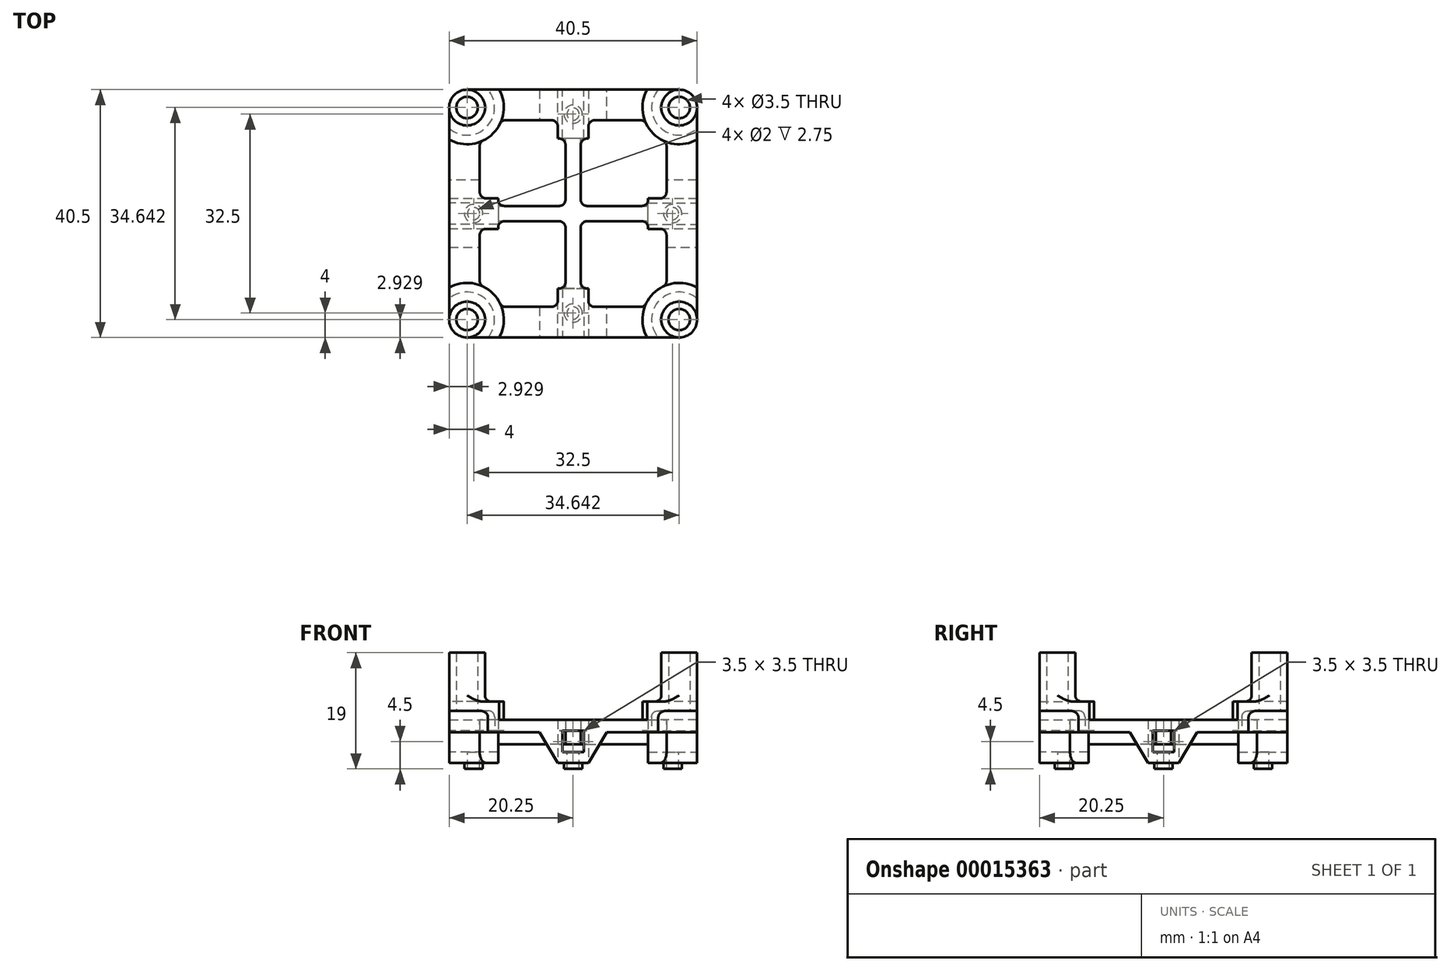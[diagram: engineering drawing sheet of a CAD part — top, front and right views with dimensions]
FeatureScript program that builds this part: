
annotation { "Feature Type Name" : "Feature", "Feature Type Description" : "" }
export const myFeature = defineFeature(function(context is Context, id is Id, definition is map)
    precondition{}
    {
        {
            var Q0;
            Q0=qCreatedBy(makeId("Top.planeOp"),FACE);
            var sketch = newSketch(context, id + "F0", { "sketchPlane" : qUnion([Q0])});
            skLineSegment(sketch, "E0.top", {"start": v(2.93, 40.5) * mm, "end": v(37.57, 40.5) * mm});
            skLineSegment(sketch, "E0.left", {"start": v(0, 2.93) * mm, "end": v(0, 37.57) * mm});
            skLineSegment(sketch, "E0.right", {"start": v(40.5, 2.93) * mm, "end": v(40.5, 37.57) * mm});
            skLineSegment(sketch, "E1", {"start": v(2.93, 0) * mm, "end": v(5, 0) * mm, "construction": true});
            skLineSegment(sketch, "E2", {"start": v(5, 0) * mm, "end": v(5, 5) * mm, "construction": true});
            skLineSegment(sketch, "E3.MirrorCS", {"start": v(40.5, 35.5) * mm, "end": v(35.5, 35.5) * mm, "construction": true});
            skLineSegment(sketch, "E4.MirrorCS", {"start": v(40.5, 37.57) * mm, "end": v(40.5, 35.5) * mm, "construction": true});
            skLineSegment(sketch, "E5", {"start": v(5, 35.5) * mm, "end": v(0, 40.5) * mm, "construction": true});
            skCircle(sketch, "E6", {"center": v(2.93, 37.57) * mm, "radius": 2.93 * mm});
            skLineSegment(sketch, "E7", {"start": v(35.5, 35.5) * mm, "end": v(40.5, 40.5) * mm, "construction": true});
            skLineSegment(sketch, "E8", {"start": v(35.5, 5) * mm, "end": v(40.5, 0) * mm, "construction": true});
            skLineSegment(sketch, "E9", {"start": v(5, 5) * mm, "end": v(0, 0) * mm, "construction": true});
            skCircle(sketch, "E10", {"center": v(37.57, 37.57) * mm, "radius": 2.93 * mm});
            skCircle(sketch, "E11", {"center": v(37.57, 2.93) * mm, "radius": 2.93 * mm});
            skCircle(sketch, "E12", {"center": v(2.93, 2.93) * mm, "radius": 2.93 * mm});
            skPoint(sketch, "E13.orphan", {"position": v(40.5, 40.5) * mm});
            skLineSegment(sketch, "E14", {"start": v(22.75, 35.5) * mm, "end": v(22.75, 35.5) * mm});
            skLineSegment(sketch, "E15", {"start": v(5, 35.5) * mm, "end": v(5, 22.75) * mm});
            skLineSegment(sketch, "E16", {"start": v(5, 5) * mm, "end": v(17.75, 5) * mm});
            skLineSegment(sketch, "E17", {"start": v(35.5, 35.5) * mm, "end": v(35.5, 22.75) * mm});
            skLineSegment(sketch, "E18", {"start": v(35.5, 35.5) * mm, "end": v(22.75, 35.5) * mm});
            skLineSegment(sketch, "E19.left", {"start": v(5, 5) * mm, "end": v(5, 17.75) * mm});
            skLineSegment(sketch, "E20.bottom", {"start": v(5, 35.5) * mm, "end": v(17.75, 35.5) * mm});
            skLineSegment(sketch, "E21.bottom", {"start": v(35.5, 5) * mm, "end": v(22.75, 5) * mm});
            skLineSegment(sketch, "E21.left", {"start": v(35.5, 5) * mm, "end": v(35.5, 17.75) * mm});
            skLineSegment(sketch, "E22.trimOffspring", {"start": v(35.5, 17.75) * mm, "end": v(35.5, 5) * mm});
            skLineSegment(sketch, "E23.trimOffspring", {"start": v(5, 17.75) * mm, "end": v(5, 5) * mm});
            skLineSegment(sketch, "E24.trimOffspring", {"start": v(17.75, 35.5) * mm, "end": v(5, 35.5) * mm});
            skLineSegment(sketch, "E25.trimOffspring", {"start": v(22.75, 5) * mm, "end": v(35.5, 5) * mm});
            skPoint(sketch, "E26.orphan", {"position": v(20.25, 0) * mm});
            skLineSegment(sketch, "E27", {"start": v(2.93, 0) * mm, "end": v(40.5, 0) * mm});
            skLineSegment(sketch, "E28", {"start": v(22.75, 5) * mm, "end": v(17.75, 5) * mm});
            skLineSegment(sketch, "E29", {"start": v(5, 22.75) * mm, "end": v(5, 17.75) * mm});
            skLineSegment(sketch, "E30", {"start": v(17.75, 35.5) * mm, "end": v(22.75, 35.5) * mm});
            skLineSegment(sketch, "E31", {"start": v(35.5, 22.75) * mm, "end": v(35.5, 17.75) * mm});
            skSolve(sketch);
        }
        {
            var Q0;
            Q0=qSketchRegion(id+"F0",true);
            extrude(context, id + "F1", {"entities" : qUnion([Q0]), "depth" : 2 * mm});
        }
        {
            var Q0;
            Q0=makeQuery(id+"F1.opExtrude","CAP_FACE",FACE,{"disambiguationData":[OSD([sQuery(id+"F0.wireOp",EDGE,"E0.top"),sQuery(id+"F0.wireOp",EDGE,"E0.left"),sQuery(id+"F0.wireOp",EDGE,"E0.right"),sQuery(id+"F0.wireOp",EDGE,"E6"),sQuery(id+"F0.wireOp",EDGE,"E10"),sQuery(id+"F0.wireOp",EDGE,"E11"),sQuery(id+"F0.wireOp",EDGE,"E12"),sQuery(id+"F0.wireOp",EDGE,"E16"),sQuery(id+"F0.wireOp",EDGE,"E15"),sQuery(id+"F0.wireOp",EDGE,"E18"),sQuery(id+"F0.wireOp",EDGE,"E17"),sQuery(id+"F0.wireOp",EDGE,"E22.trimOffspring"),sQuery(id+"F0.wireOp",EDGE,"E23.trimOffspring"),sQuery(id+"F0.wireOp",EDGE,"E24.trimOffspring"),sQuery(id+"F0.wireOp",EDGE,"E25.trimOffspring"),sQuery(id+"F0.wireOp",EDGE,"E27"),sQuery(id+"F0.wireOp",EDGE,"E28"),sQuery(id+"F0.wireOp",EDGE,"E29"),sQuery(id+"F0.wireOp",EDGE,"E30"),sQuery(id+"F0.wireOp",EDGE,"E31")])],"isStart":false});
            var sketch = newSketch(context, id + "F2", { "sketchPlane" : qUnion([Q0])});
            skLineSegment(sketch, "E32", {"start": v(20.25, 0) * mm, "end": v(20.25, 40.5) * mm, "construction": true});
            skLineSegment(sketch, "E33", {"start": v(0, 20.25) * mm, "end": v(40.5, 20.25) * mm, "construction": true});
            skLineSegment(sketch, "E34", {"start": v(17.75, 40.5) * mm, "end": v(22.75, 40.5) * mm});
            skLineSegment(sketch, "E35", {"start": v(0, 17.75) * mm, "end": v(0, 22.75) * mm});
            skLineSegment(sketch, "E36", {"start": v(17.75, 0) * mm, "end": v(22.75, 0) * mm});
            skLineSegment(sketch, "E37", {"start": v(40.5, 17.75) * mm, "end": v(40.5, 22.75) * mm});
            skLineSegment(sketch, "E38", {"start": v(40.5, 17.75) * mm, "end": v(22.75, 17.75) * mm});
            skLineSegment(sketch, "E39", {"start": v(22.75, 17.75) * mm, "end": v(22.75, 0) * mm});
            skLineSegment(sketch, "E40", {"start": v(17.75, 0) * mm, "end": v(17.75, 17.75) * mm});
            skLineSegment(sketch, "E41", {"start": v(17.75, 17.75) * mm, "end": v(0, 17.75) * mm});
            skLineSegment(sketch, "E42", {"start": v(0, 22.75) * mm, "end": v(17.75, 22.75) * mm});
            skLineSegment(sketch, "E43", {"start": v(17.75, 22.75) * mm, "end": v(17.75, 40.5) * mm});
            skLineSegment(sketch, "E44", {"start": v(22.75, 40.5) * mm, "end": v(22.75, 22.75) * mm});
            skLineSegment(sketch, "E45", {"start": v(22.75, 22.75) * mm, "end": v(40.5, 22.75) * mm});
            skSolve(sketch);
        }
        {
            var Q0;
            Q0=qSketchRegion(id+"F2",true);
            extrude(context, id + "F3", {"entities" : qUnion([Q0]), "operationType" : NewBodyOperationType.ADD, "oppositeDirection" : true, "depth" : 7 * mm});
        }
        {
            var Q0;
            Q0=makeQuery(id+"F3.boolean.opBoolean","MERGE",FACE,{"derivedFrom":[makeQuery(id+"F1.opExtrude","SWEPT_FACE",FACE,{"disambiguationData":[OSD([sQuery(id+"F0.wireOp",EDGE,"E27")])]}),makeQuery(id+"F3.opExtrude","SWEPT_FACE",FACE,{"disambiguationData":[OSD([sQuery(id+"F2.wireOp",EDGE,"E36")])]})]});
            var sketch = newSketch(context, id + "F4", { "sketchPlane" : qUnion([Q0])});
            skLineSegment(sketch, "E46", {"start": v(22.75, -5) * mm, "end": v(17.75, 2) * mm, "construction": true});
            skLineSegment(sketch, "E47", {"start": v(17.75, -5) * mm, "end": v(22.75, 2) * mm, "construction": true});
            skLineSegment(sketch, "E48.rect.bottom", {"start": v(18.5, -3.25) * mm, "end": v(22, -3.25) * mm});
            skLineSegment(sketch, "E48.rect.top", {"start": v(18.5, 0.25) * mm, "end": v(22, 0.25) * mm});
            skLineSegment(sketch, "E48.rect.left", {"start": v(18.5, -3.25) * mm, "end": v(18.5, 0.25) * mm});
            skLineSegment(sketch, "E48.rect.right", {"start": v(22, -3.25) * mm, "end": v(22, 0.25) * mm});
            skPoint(sketch, "E48.rect.middle", {"position": v(20.25, -1.5) * mm});
            skSolve(sketch);
        }
        {
            var Q0;
            Q0=qSketchRegion(id+"F4",true);
            extrude(context, id + "F5", {"entities" : qUnion([Q0]), "operationType" : NewBodyOperationType.REMOVE, "oppositeDirection" : true, "depth" : 8 * mm});
        }
        {
            var Q0;
            Q0=makeQuery(id+"F3.boolean.opBoolean","MERGE",FACE,{"derivedFrom":[makeQuery(id+"F1.opExtrude","SWEPT_FACE",FACE,{"disambiguationData":[OSD([sQuery(id+"F0.wireOp",EDGE,"E0.right")])]}),makeQuery(id+"F3.opExtrude","SWEPT_FACE",FACE,{"disambiguationData":[OSD([sQuery(id+"F2.wireOp",EDGE,"E37")])]})]});
            var sketch = newSketch(context, id + "F6", { "sketchPlane" : qUnion([Q0])});
            skLineSegment(sketch, "E49", {"start": v(17.75, -5) * mm, "end": v(22.75, 2) * mm, "construction": true});
            skLineSegment(sketch, "E50", {"start": v(22.75, -5) * mm, "end": v(17.75, 2) * mm, "construction": true});
            skLineSegment(sketch, "E51.rect.bottom", {"start": v(18.5, -3.25) * mm, "end": v(22, -3.25) * mm});
            skLineSegment(sketch, "E51.rect.top", {"start": v(18.5, 0.25) * mm, "end": v(22, 0.25) * mm});
            skLineSegment(sketch, "E51.rect.left", {"start": v(18.5, -3.25) * mm, "end": v(18.5, 0.25) * mm});
            skLineSegment(sketch, "E51.rect.right", {"start": v(22, -3.25) * mm, "end": v(22, 0.25) * mm});
            skPoint(sketch, "E51.rect.middle", {"position": v(20.25, -1.5) * mm});
            skSolve(sketch);
        }
        {
            var Q0;
            Q0=qSketchRegion(id+"F6",true);
            extrude(context, id + "F7", {"entities" : qUnion([Q0]), "operationType" : NewBodyOperationType.REMOVE, "oppositeDirection" : true, "depth" : 8 * mm});
        }
        {
            var Q0;
            Q0=makeQuery(id+"F3.boolean.opBoolean","MERGE",FACE,{"derivedFrom":[makeQuery(id+"F1.opExtrude","SWEPT_FACE",FACE,{"disambiguationData":[OSD([sQuery(id+"F0.wireOp",EDGE,"E0.top")])]}),makeQuery(id+"F3.opExtrude","SWEPT_FACE",FACE,{"disambiguationData":[OSD([sQuery(id+"F2.wireOp",EDGE,"E34")])]})]});
            var sketch = newSketch(context, id + "F8", { "sketchPlane" : qUnion([Q0])});
            skLineSegment(sketch, "E52", {"start": v(-17.75, -5) * mm, "end": v(-22.75, 2) * mm, "construction": true});
            skLineSegment(sketch, "E53", {"start": v(-22.75, -5) * mm, "end": v(-17.75, 2) * mm, "construction": true});
            skLineSegment(sketch, "E54.rect.bottom", {"start": v(-22, -3.25) * mm, "end": v(-18.5, -3.25) * mm});
            skLineSegment(sketch, "E54.rect.top", {"start": v(-22, 0.25) * mm, "end": v(-18.5, 0.25) * mm});
            skLineSegment(sketch, "E54.rect.left", {"start": v(-22, -3.25) * mm, "end": v(-22, 0.25) * mm});
            skLineSegment(sketch, "E54.rect.right", {"start": v(-18.5, -3.25) * mm, "end": v(-18.5, 0.25) * mm});
            skPoint(sketch, "E54.rect.middle", {"position": v(-20.25, -1.5) * mm});
            skSolve(sketch);
        }
        {
            var Q0;
            Q0=qSketchRegion(id+"F8",true);
            extrude(context, id + "F9", {"entities" : qUnion([Q0]), "operationType" : NewBodyOperationType.REMOVE, "oppositeDirection" : true, "depth" : 8 * mm});
        }
        {
            var Q0;
            Q0=makeQuery(id+"F3.boolean.opBoolean","MERGE",FACE,{"derivedFrom":[makeQuery(id+"F1.opExtrude","SWEPT_FACE",FACE,{"disambiguationData":[OSD([sQuery(id+"F0.wireOp",EDGE,"E0.left")])]}),makeQuery(id+"F3.opExtrude","SWEPT_FACE",FACE,{"disambiguationData":[OSD([sQuery(id+"F2.wireOp",EDGE,"E35")])]})]});
            var sketch = newSketch(context, id + "F10", { "sketchPlane" : qUnion([Q0])});
            skLineSegment(sketch, "E55", {"start": v(-22.75, -5) * mm, "end": v(-17.75, 2) * mm, "construction": true});
            skLineSegment(sketch, "E56", {"start": v(-17.75, -5) * mm, "end": v(-22.75, -1.43) * mm, "construction": true});
            skLineSegment(sketch, "E57.rect.bottom", {"start": v(-22, -3.25) * mm, "end": v(-18.5, -3.25) * mm});
            skLineSegment(sketch, "E57.rect.top", {"start": v(-22, 0.25) * mm, "end": v(-18.5, 0.25) * mm});
            skLineSegment(sketch, "E57.rect.left", {"start": v(-22, -3.25) * mm, "end": v(-22, 0.25) * mm});
            skLineSegment(sketch, "E57.rect.right", {"start": v(-18.5, -3.25) * mm, "end": v(-18.5, 0.25) * mm});
            skPoint(sketch, "E57.rect.middle", {"position": v(-20.25, -1.5) * mm});
            skSolve(sketch);
        }
        {
            var Q0;
            Q0=qSketchRegion(id+"F10",true);
            extrude(context, id + "F11", {"entities" : qUnion([Q0]), "operationType" : NewBodyOperationType.REMOVE, "oppositeDirection" : true, "depth" : 8 * mm});
        }
        {
            var Q0;
            Q0=makeQuery(id+"F3.opExtrude","CAP_FACE",FACE,{"disambiguationData":[OSD([sQuery(id+"F2.wireOp",EDGE,"E34"),sQuery(id+"F2.wireOp",EDGE,"E35"),sQuery(id+"F2.wireOp",EDGE,"E36"),sQuery(id+"F2.wireOp",EDGE,"E37"),sQuery(id+"F2.wireOp",EDGE,"E38"),sQuery(id+"F2.wireOp",EDGE,"E39"),sQuery(id+"F2.wireOp",EDGE,"E40"),sQuery(id+"F2.wireOp",EDGE,"E41"),sQuery(id+"F2.wireOp",EDGE,"E42"),sQuery(id+"F2.wireOp",EDGE,"E43"),sQuery(id+"F2.wireOp",EDGE,"E44"),sQuery(id+"F2.wireOp",EDGE,"E45")])],"isStart":false});
            var sketch = newSketch(context, id + "F12", { "sketchPlane" : qUnion([Q0])});
            skLineSegment(sketch, "E58", {"start": v(0, -22.75) * mm, "end": v(8, -22.75) * mm, "construction": true});
            skLineSegment(sketch, "E59", {"start": v(8, -22.75) * mm, "end": v(8, -17.75) * mm});
            skLineSegment(sketch, "E60", {"start": v(22.75, -40.5) * mm, "end": v(22.75, -32.5) * mm, "construction": true});
            skLineSegment(sketch, "E61", {"start": v(22.75, -32.5) * mm, "end": v(17.75, -32.5) * mm});
            skLineSegment(sketch, "E62", {"start": v(40.5, -17.75) * mm, "end": v(32.5, -17.75) * mm, "construction": true});
            skLineSegment(sketch, "E63", {"start": v(32.5, -17.75) * mm, "end": v(32.5, -22.75) * mm});
            skLineSegment(sketch, "E64", {"start": v(22.75, 0) * mm, "end": v(22.75, -8) * mm, "construction": true});
            skLineSegment(sketch, "E65", {"start": v(22.75, -8) * mm, "end": v(17.75, -8) * mm});
            skLineSegment(sketch, "E66", {"start": v(32.5, -22.75) * mm, "end": v(22.75, -22.75) * mm});
            skLineSegment(sketch, "E67", {"start": v(22.75, -22.75) * mm, "end": v(22.75, -32.5) * mm});
            skLineSegment(sketch, "E68", {"start": v(17.75, -32.5) * mm, "end": v(17.75, -22.75) * mm});
            skLineSegment(sketch, "E69", {"start": v(17.75, -22.75) * mm, "end": v(8, -22.75) * mm});
            skLineSegment(sketch, "E70", {"start": v(8, -17.75) * mm, "end": v(17.75, -17.75) * mm});
            skLineSegment(sketch, "E71", {"start": v(17.75, -17.75) * mm, "end": v(17.75, -8) * mm});
            skLineSegment(sketch, "E72", {"start": v(22.75, -8) * mm, "end": v(22.75, -17.75) * mm});
            skLineSegment(sketch, "E73", {"start": v(22.75, -17.75) * mm, "end": v(32.5, -17.75) * mm});
            skSolve(sketch);
        }
        {
            var Q0;
            Q0=qSketchRegion(id+"F12",true);
            extrude(context, id + "F13", {"entities" : qUnion([Q0]), "operationType" : NewBodyOperationType.REMOVE, "oppositeDirection" : true, "depth" : 3 * mm});
        }
        {
            var Q0;
            {var subQ0=sQuery(id+"F0.wireOp",EDGE,"E0.top");var subQ1=sQuery(id+"F0.wireOp",EDGE,"E0.left");var subQ2=sQuery(id+"F0.wireOp",EDGE,"E0.right");var subQ3=sQuery(id+"F0.wireOp",EDGE,"E6");var subQ4=sQuery(id+"F0.wireOp",EDGE,"E10");var subQ5=sQuery(id+"F0.wireOp",EDGE,"E11");var subQ6=sQuery(id+"F0.wireOp",EDGE,"E12");var subQ7=sQuery(id+"F0.wireOp",EDGE,"E16");var subQ8=sQuery(id+"F0.wireOp",EDGE,"E15");var subQ9=sQuery(id+"F0.wireOp",EDGE,"E18");var subQ10=sQuery(id+"F0.wireOp",EDGE,"E17");var subQ11=sQuery(id+"F0.wireOp",EDGE,"E22.trimOffspring");var subQ12=sQuery(id+"F0.wireOp",EDGE,"E23.trimOffspring");var subQ13=sQuery(id+"F0.wireOp",EDGE,"E24.trimOffspring");var subQ14=sQuery(id+"F0.wireOp",EDGE,"E25.trimOffspring");var subQ15=sQuery(id+"F0.wireOp",EDGE,"E27");var subQ16=sQuery(id+"F0.wireOp",EDGE,"E28");var subQ17=sQuery(id+"F0.wireOp",EDGE,"E29");var subQ18=sQuery(id+"F0.wireOp",EDGE,"E30");var subQ19=sQuery(id+"F0.wireOp",EDGE,"E31");var subQ20=sQuery(id+"F2.wireOp",EDGE,"E34");var subQ21=sQuery(id+"F2.wireOp",EDGE,"E35");var subQ22=sQuery(id+"F2.wireOp",EDGE,"E36");var subQ23=sQuery(id+"F2.wireOp",EDGE,"E37");var subQ24=sQuery(id+"F2.wireOp",EDGE,"E38");var subQ25=sQuery(id+"F2.wireOp",EDGE,"E39");var subQ26=sQuery(id+"F2.wireOp",EDGE,"E40");var subQ27=sQuery(id+"F2.wireOp",EDGE,"E41");var subQ28=sQuery(id+"F2.wireOp",EDGE,"E42");var subQ29=sQuery(id+"F2.wireOp",EDGE,"E43");var subQ30=sQuery(id+"F2.wireOp",EDGE,"E44");var subQ31=sQuery(id+"F2.wireOp",EDGE,"E45");Q0=makeQuery(id+"F5kflJwKjGJNZqC_1.boolean.opBoolean","SPLIT",FACE,{"disambiguationData":[TD([makeQuery(id+"F1.opExtrude","SWEPT_FACE",FACE,{"disambiguationData":[OSD([subQ0])]})])],"derivedFrom":makeQuery(id+"F3.boolean.opBoolean","MERGE",FACE,{"derivedFrom":[makeQuery(id+"F1.opExtrude","CAP_FACE",FACE,{"disambiguationData":[OSD([subQ0,subQ1,subQ2,subQ3,subQ4,subQ5,subQ6,subQ7,subQ8,subQ9,subQ10,subQ11,subQ12,subQ13,subQ14,subQ15,subQ16,subQ17,subQ18,subQ19])],"isStart":false}),makeQuery(id+"F3.opExtrude","CAP_FACE",FACE,{"disambiguationData":[OSD([subQ20,subQ21,subQ22,subQ23,subQ24,subQ25,subQ26,subQ27,subQ28,subQ29,subQ30,subQ31])],"isStart":true})]})});}
            var sketch = newSketch(context, id + "F14", { "sketchPlane" : qUnion([Q0])});
            skCircle(sketch, "E74", {"center": v(37.57, 37.57) * mm, "radius": 2.93 * mm});
            skCircle(sketch, "E75", {"center": v(37.57, 2.93) * mm, "radius": 2.93 * mm});
            skCircle(sketch, "E76", {"center": v(2.93, 2.93) * mm, "radius": 2.93 * mm});
            skCircle(sketch, "E77", {"center": v(2.93, 37.57) * mm, "radius": 2.93 * mm});
            skSolve(sketch);
        }
        {
            var Q0;
            Q0=qSketchRegion(id+"F14",true);
            extrude(context, id + "F15", {"entities" : qUnion([Q0]), "operationType" : NewBodyOperationType.ADD, "depth" : 11 * mm});
        }
        {
            var Q0;
            {var subQ0=sQuery(id+"F2.wireOp",EDGE,"E41");var subQ1=sQuery(id+"F2.wireOp",EDGE,"E35");var subQ2=sQuery(id+"F2.wireOp",EDGE,"E42");Q0=makeQuery(id+"F13.boolean.opBoolean","SPLIT",FACE,{"disambiguationData":[TD([makeQuery(id+"F1.opExtrude","SWEPT_FACE",FACE,{"disambiguationData":[OSD([sQuery(id+"F0.wireOp",EDGE,"E0.left")])]})])],"derivedFrom":makeQuery(id+"F3.opExtrude","CAP_FACE",FACE,{"disambiguationData":[OSD([sQuery(id+"F2.wireOp",EDGE,"E34"),subQ1,sQuery(id+"F2.wireOp",EDGE,"E36"),sQuery(id+"F2.wireOp",EDGE,"E37"),sQuery(id+"F2.wireOp",EDGE,"E38"),sQuery(id+"F2.wireOp",EDGE,"E39"),sQuery(id+"F2.wireOp",EDGE,"E40"),subQ0,subQ2,sQuery(id+"F2.wireOp",EDGE,"E43"),sQuery(id+"F2.wireOp",EDGE,"E44"),sQuery(id+"F2.wireOp",EDGE,"E45")])],"isStart":false})});}
            var sketch = newSketch(context, id + "F16", { "sketchPlane" : qUnion([Q0])});
            skLineSegment(sketch, "E78", {"start": v(8, -22.75) * mm, "end": v(0, -17.75) * mm, "construction": true});
            skCircle(sketch, "E79", {"center": v(4, -20.25) * mm, "radius": 1 * mm});
            skCircle(sketch, "E80", {"center": v(4, -20.25) * mm, "radius": 1.5 * mm});
            skSolve(sketch);
        }
        {
            var Q0;
            Q0=qSketchRegion(id+"F16",true);
            extrude(context, id + "F17", {"entities" : qUnion([Q0]), "operationType" : NewBodyOperationType.ADD, "depth" : 1 * mm});
        }
        {
            var Q0;
            {var subQ0=sQuery(id+"F2.wireOp",EDGE,"E43");var subQ1=sQuery(id+"F2.wireOp",EDGE,"E34");var subQ2=sQuery(id+"F2.wireOp",EDGE,"E44");Q0=makeQuery(id+"F13.boolean.opBoolean","SPLIT",FACE,{"disambiguationData":[TD([makeQuery(id+"F1.opExtrude","SWEPT_FACE",FACE,{"disambiguationData":[OSD([sQuery(id+"F0.wireOp",EDGE,"E0.top")])]})])],"derivedFrom":makeQuery(id+"F3.opExtrude","CAP_FACE",FACE,{"disambiguationData":[OSD([subQ1,sQuery(id+"F2.wireOp",EDGE,"E35"),sQuery(id+"F2.wireOp",EDGE,"E36"),sQuery(id+"F2.wireOp",EDGE,"E37"),sQuery(id+"F2.wireOp",EDGE,"E38"),sQuery(id+"F2.wireOp",EDGE,"E39"),sQuery(id+"F2.wireOp",EDGE,"E40"),sQuery(id+"F2.wireOp",EDGE,"E41"),sQuery(id+"F2.wireOp",EDGE,"E42"),subQ0,subQ2,sQuery(id+"F2.wireOp",EDGE,"E45")])],"isStart":false})});}
            var sketch = newSketch(context, id + "F18", { "sketchPlane" : qUnion([Q0])});
            skLineSegment(sketch, "E81", {"start": v(22.75, -32.5) * mm, "end": v(17.75, -40.5) * mm});
            skCircle(sketch, "E82", {"center": v(20.25, -36.5) * mm, "radius": 1 * mm});
            skCircle(sketch, "E83", {"center": v(20.25, -36.5) * mm, "radius": 1.5 * mm});
            skSolve(sketch);
        }
        {
            var Q0;
            Q0=qSketchRegion(id+"F18",true);
            extrude(context, id + "F19", {"entities" : qUnion([Q0]), "operationType" : NewBodyOperationType.ADD, "depth" : 1 * mm});
        }
        {
            var Q0;
            {var subQ0=sQuery(id+"F2.wireOp",EDGE,"E45");var subQ1=sQuery(id+"F2.wireOp",EDGE,"E37");var subQ2=sQuery(id+"F2.wireOp",EDGE,"E38");Q0=makeQuery(id+"F13.boolean.opBoolean","SPLIT",FACE,{"disambiguationData":[TD([makeQuery(id+"F1.opExtrude","SWEPT_FACE",FACE,{"disambiguationData":[OSD([sQuery(id+"F0.wireOp",EDGE,"E0.right")])]})])],"derivedFrom":makeQuery(id+"F3.opExtrude","CAP_FACE",FACE,{"disambiguationData":[OSD([sQuery(id+"F2.wireOp",EDGE,"E34"),sQuery(id+"F2.wireOp",EDGE,"E35"),sQuery(id+"F2.wireOp",EDGE,"E36"),subQ1,subQ2,sQuery(id+"F2.wireOp",EDGE,"E39"),sQuery(id+"F2.wireOp",EDGE,"E40"),sQuery(id+"F2.wireOp",EDGE,"E41"),sQuery(id+"F2.wireOp",EDGE,"E42"),sQuery(id+"F2.wireOp",EDGE,"E43"),sQuery(id+"F2.wireOp",EDGE,"E44"),subQ0])],"isStart":false})});}
            var sketch = newSketch(context, id + "F20", { "sketchPlane" : qUnion([Q0])});
            skLineSegment(sketch, "E84", {"start": v(32.5, -17.75) * mm, "end": v(40.5, -22.75) * mm});
            skCircle(sketch, "E85", {"center": v(36.5, -20.25) * mm, "radius": 1 * mm});
            skCircle(sketch, "E86", {"center": v(36.5, -20.25) * mm, "radius": 1.5 * mm});
            skSolve(sketch);
        }
        {
            var Q0;
            Q0=qSketchRegion(id+"F20",true);
            extrude(context, id + "F21", {"entities" : qUnion([Q0]), "operationType" : NewBodyOperationType.ADD, "depth" : 1 * mm});
        }
        {
            var Q0;
            {var subQ0=sQuery(id+"F2.wireOp",EDGE,"E40");var subQ1=sQuery(id+"F2.wireOp",EDGE,"E39");var subQ2=sQuery(id+"F2.wireOp",EDGE,"E36");Q0=makeQuery(id+"F13.boolean.opBoolean","SPLIT",FACE,{"disambiguationData":[TD([makeQuery(id+"F1.opExtrude","SWEPT_FACE",FACE,{"disambiguationData":[OSD([sQuery(id+"F0.wireOp",EDGE,"E27")])]})])],"derivedFrom":makeQuery(id+"F3.opExtrude","CAP_FACE",FACE,{"disambiguationData":[OSD([sQuery(id+"F2.wireOp",EDGE,"E34"),sQuery(id+"F2.wireOp",EDGE,"E35"),subQ2,sQuery(id+"F2.wireOp",EDGE,"E37"),sQuery(id+"F2.wireOp",EDGE,"E38"),subQ1,subQ0,sQuery(id+"F2.wireOp",EDGE,"E41"),sQuery(id+"F2.wireOp",EDGE,"E42"),sQuery(id+"F2.wireOp",EDGE,"E43"),sQuery(id+"F2.wireOp",EDGE,"E44"),sQuery(id+"F2.wireOp",EDGE,"E45")])],"isStart":false})});}
            var sketch = newSketch(context, id + "F22", { "sketchPlane" : qUnion([Q0])});
            skLineSegment(sketch, "E87", {"start": v(17.75, -8) * mm, "end": v(22.75, 0) * mm});
            skCircle(sketch, "E88", {"center": v(20.25, -4) * mm, "radius": 1 * mm});
            skCircle(sketch, "E89", {"center": v(20.25, -4) * mm, "radius": 1.5 * mm});
            skSolve(sketch);
        }
        {
            var Q0;
            Q0=qSketchRegion(id+"F22",true);
            extrude(context, id + "F23", {"entities" : qUnion([Q0]), "operationType" : NewBodyOperationType.ADD, "depth" : 1 * mm});
        }
        {
            var Q0;
            {var subQ0=sQuery(id+"F0.wireOp",EDGE,"E0.left");var subQ1=sQuery(id+"F0.wireOp",EDGE,"E12");var subQ2=sQuery(id+"F0.wireOp",EDGE,"E16");var subQ3=sQuery(id+"F0.wireOp",EDGE,"E15");var subQ4=sQuery(id+"F0.wireOp",EDGE,"E23.trimOffspring");var subQ5=sQuery(id+"F0.wireOp",EDGE,"E25.trimOffspring");var subQ6=sQuery(id+"F0.wireOp",EDGE,"E27");var subQ7=sQuery(id+"F0.wireOp",EDGE,"E28");var subQ8=sQuery(id+"F0.wireOp",EDGE,"E29");Q0=makeQuery(id+"F3.boolean.opBoolean","SPLIT",FACE,{"disambiguationData":[TD([makeQuery(id+"F1.opExtrude","SWEPT_FACE",FACE,{"disambiguationData":[OSD([subQ1])]})])],"derivedFrom":makeQuery(id+"F1.opExtrude","CAP_FACE",FACE,{"disambiguationData":[OSD([sQuery(id+"F0.wireOp",EDGE,"E0.top"),subQ0,sQuery(id+"F0.wireOp",EDGE,"E0.right"),sQuery(id+"F0.wireOp",EDGE,"E6"),sQuery(id+"F0.wireOp",EDGE,"E10"),sQuery(id+"F0.wireOp",EDGE,"E11"),subQ1,subQ2,subQ3,sQuery(id+"F0.wireOp",EDGE,"E18"),sQuery(id+"F0.wireOp",EDGE,"E17"),sQuery(id+"F0.wireOp",EDGE,"E22.trimOffspring"),subQ4,sQuery(id+"F0.wireOp",EDGE,"E24.trimOffspring"),subQ5,subQ6,subQ7,subQ8,sQuery(id+"F0.wireOp",EDGE,"E30"),sQuery(id+"F0.wireOp",EDGE,"E31")])],"isStart":true})});}
            var sketch = newSketch(context, id + "F24", { "sketchPlane" : qUnion([Q0])});
            skCircle(sketch, "E90", {"center": v(2.93, -2.93) * mm, "radius": 1.75 * mm});
            skSolve(sketch);
        }
        {
            var Q0;
            Q0=qSketchRegion(id+"F24",true);
            extrude(context, id + "F25", {"entities" : qUnion([Q0]), "operationType" : NewBodyOperationType.REMOVE, "oppositeDirection" : true, "depth" : 25 * mm});
        }
        {
            var Q0;
            {var subQ0=sQuery(id+"F0.wireOp",EDGE,"E0.right");var subQ1=sQuery(id+"F0.wireOp",EDGE,"E11");var subQ2=sQuery(id+"F0.wireOp",EDGE,"E16");var subQ3=sQuery(id+"F0.wireOp",EDGE,"E17");var subQ4=sQuery(id+"F0.wireOp",EDGE,"E22.trimOffspring");var subQ5=sQuery(id+"F0.wireOp",EDGE,"E25.trimOffspring");var subQ6=sQuery(id+"F0.wireOp",EDGE,"E27");var subQ7=sQuery(id+"F0.wireOp",EDGE,"E28");var subQ8=sQuery(id+"F0.wireOp",EDGE,"E31");Q0=makeQuery(id+"F3.boolean.opBoolean","SPLIT",FACE,{"disambiguationData":[TD([makeQuery(id+"F1.opExtrude","SWEPT_FACE",FACE,{"disambiguationData":[OSD([subQ1])]})])],"derivedFrom":makeQuery(id+"F1.opExtrude","CAP_FACE",FACE,{"disambiguationData":[OSD([sQuery(id+"F0.wireOp",EDGE,"E0.top"),sQuery(id+"F0.wireOp",EDGE,"E0.left"),subQ0,sQuery(id+"F0.wireOp",EDGE,"E6"),sQuery(id+"F0.wireOp",EDGE,"E10"),subQ1,sQuery(id+"F0.wireOp",EDGE,"E12"),subQ2,sQuery(id+"F0.wireOp",EDGE,"E15"),sQuery(id+"F0.wireOp",EDGE,"E18"),subQ3,subQ4,sQuery(id+"F0.wireOp",EDGE,"E23.trimOffspring"),sQuery(id+"F0.wireOp",EDGE,"E24.trimOffspring"),subQ5,subQ6,subQ7,sQuery(id+"F0.wireOp",EDGE,"E29"),sQuery(id+"F0.wireOp",EDGE,"E30"),subQ8])],"isStart":true})});}
            var sketch = newSketch(context, id + "F26", { "sketchPlane" : qUnion([Q0])});
            skCircle(sketch, "E91", {"center": v(37.57, -2.93) * mm, "radius": 1.75 * mm});
            skSolve(sketch);
        }
        {
            var Q0;
            Q0=qSketchRegion(id+"F26",true);
            extrude(context, id + "F27", {"entities" : qUnion([Q0]), "operationType" : NewBodyOperationType.REMOVE, "oppositeDirection" : true, "depth" : 25 * mm});
        }
        {
            var Q0;
            {var subQ0=sQuery(id+"F0.wireOp",EDGE,"E0.top");var subQ1=sQuery(id+"F0.wireOp",EDGE,"E0.left");var subQ2=sQuery(id+"F0.wireOp",EDGE,"E6");var subQ3=sQuery(id+"F0.wireOp",EDGE,"E15");var subQ4=sQuery(id+"F0.wireOp",EDGE,"E18");var subQ5=sQuery(id+"F0.wireOp",EDGE,"E23.trimOffspring");var subQ6=sQuery(id+"F0.wireOp",EDGE,"E24.trimOffspring");var subQ7=sQuery(id+"F0.wireOp",EDGE,"E29");var subQ8=sQuery(id+"F0.wireOp",EDGE,"E30");Q0=makeQuery(id+"F3.boolean.opBoolean","SPLIT",FACE,{"disambiguationData":[TD([makeQuery(id+"F1.opExtrude","SWEPT_FACE",FACE,{"disambiguationData":[OSD([subQ2])]})])],"derivedFrom":makeQuery(id+"F1.opExtrude","CAP_FACE",FACE,{"disambiguationData":[OSD([subQ0,subQ1,sQuery(id+"F0.wireOp",EDGE,"E0.right"),subQ2,sQuery(id+"F0.wireOp",EDGE,"E10"),sQuery(id+"F0.wireOp",EDGE,"E11"),sQuery(id+"F0.wireOp",EDGE,"E12"),sQuery(id+"F0.wireOp",EDGE,"E16"),subQ3,subQ4,sQuery(id+"F0.wireOp",EDGE,"E17"),sQuery(id+"F0.wireOp",EDGE,"E22.trimOffspring"),subQ5,subQ6,sQuery(id+"F0.wireOp",EDGE,"E25.trimOffspring"),sQuery(id+"F0.wireOp",EDGE,"E27"),sQuery(id+"F0.wireOp",EDGE,"E28"),subQ7,subQ8,sQuery(id+"F0.wireOp",EDGE,"E31")])],"isStart":true})});}
            var sketch = newSketch(context, id + "F28", { "sketchPlane" : qUnion([Q0])});
            skCircle(sketch, "E92", {"center": v(2.93, -37.57) * mm, "radius": 1.75 * mm});
            skSolve(sketch);
        }
        {
            var Q0;
            Q0=qSketchRegion(id+"F28",true);
            extrude(context, id + "F29", {"entities" : qUnion([Q0]), "operationType" : NewBodyOperationType.REMOVE, "oppositeDirection" : true, "depth" : 25 * mm});
        }
        {
            var Q0;
            {var subQ0=sQuery(id+"F0.wireOp",EDGE,"E0.top");var subQ1=sQuery(id+"F0.wireOp",EDGE,"E0.right");var subQ2=sQuery(id+"F0.wireOp",EDGE,"E10");var subQ3=sQuery(id+"F0.wireOp",EDGE,"E18");var subQ4=sQuery(id+"F0.wireOp",EDGE,"E17");var subQ5=sQuery(id+"F0.wireOp",EDGE,"E22.trimOffspring");var subQ6=sQuery(id+"F0.wireOp",EDGE,"E24.trimOffspring");var subQ7=sQuery(id+"F0.wireOp",EDGE,"E30");var subQ8=sQuery(id+"F0.wireOp",EDGE,"E31");Q0=makeQuery(id+"F3.boolean.opBoolean","SPLIT",FACE,{"disambiguationData":[TD([makeQuery(id+"F1.opExtrude","SWEPT_FACE",FACE,{"disambiguationData":[OSD([subQ2])]})])],"derivedFrom":makeQuery(id+"F1.opExtrude","CAP_FACE",FACE,{"disambiguationData":[OSD([subQ0,sQuery(id+"F0.wireOp",EDGE,"E0.left"),subQ1,sQuery(id+"F0.wireOp",EDGE,"E6"),subQ2,sQuery(id+"F0.wireOp",EDGE,"E11"),sQuery(id+"F0.wireOp",EDGE,"E12"),sQuery(id+"F0.wireOp",EDGE,"E16"),sQuery(id+"F0.wireOp",EDGE,"E15"),subQ3,subQ4,subQ5,sQuery(id+"F0.wireOp",EDGE,"E23.trimOffspring"),subQ6,sQuery(id+"F0.wireOp",EDGE,"E25.trimOffspring"),sQuery(id+"F0.wireOp",EDGE,"E27"),sQuery(id+"F0.wireOp",EDGE,"E28"),sQuery(id+"F0.wireOp",EDGE,"E29"),subQ7,subQ8])],"isStart":true})});}
            var sketch = newSketch(context, id + "F30", { "sketchPlane" : qUnion([Q0])});
            skCircle(sketch, "E93", {"center": v(37.57, -37.57) * mm, "radius": 1.75 * mm});
            skSolve(sketch);
        }
        {
            var Q0;
            Q0=qSketchRegion(id+"F30",true);
            extrude(context, id + "F31", {"entities" : qUnion([Q0]), "operationType" : NewBodyOperationType.REMOVE, "oppositeDirection" : true, "depth" : 25 * mm});
        }
        {
            var Q0;
            Q0=makeQuery(id+"F3.boolean.opBoolean","MERGE",FACE,{"derivedFrom":[makeQuery(id+"F1.opExtrude","CAP_FACE",FACE,{"disambiguationData":[OSD([sQuery(id+"F0.wireOp",EDGE,"E0.top"),sQuery(id+"F0.wireOp",EDGE,"E0.left"),sQuery(id+"F0.wireOp",EDGE,"E0.right"),sQuery(id+"F0.wireOp",EDGE,"E6"),sQuery(id+"F0.wireOp",EDGE,"E10"),sQuery(id+"F0.wireOp",EDGE,"E11"),sQuery(id+"F0.wireOp",EDGE,"E12"),sQuery(id+"F0.wireOp",EDGE,"E16"),sQuery(id+"F0.wireOp",EDGE,"E15"),sQuery(id+"F0.wireOp",EDGE,"E18"),sQuery(id+"F0.wireOp",EDGE,"E17"),sQuery(id+"F0.wireOp",EDGE,"E22.trimOffspring"),sQuery(id+"F0.wireOp",EDGE,"E23.trimOffspring"),sQuery(id+"F0.wireOp",EDGE,"E24.trimOffspring"),sQuery(id+"F0.wireOp",EDGE,"E25.trimOffspring"),sQuery(id+"F0.wireOp",EDGE,"E27"),sQuery(id+"F0.wireOp",EDGE,"E28"),sQuery(id+"F0.wireOp",EDGE,"E29"),sQuery(id+"F0.wireOp",EDGE,"E30"),sQuery(id+"F0.wireOp",EDGE,"E31")])],"isStart":false}),makeQuery(id+"F3.opExtrude","CAP_FACE",FACE,{"disambiguationData":[OSD([sQuery(id+"F2.wireOp",EDGE,"E34"),sQuery(id+"F2.wireOp",EDGE,"E35"),sQuery(id+"F2.wireOp",EDGE,"E36"),sQuery(id+"F2.wireOp",EDGE,"E37"),sQuery(id+"F2.wireOp",EDGE,"E38"),sQuery(id+"F2.wireOp",EDGE,"E39"),sQuery(id+"F2.wireOp",EDGE,"E40"),sQuery(id+"F2.wireOp",EDGE,"E41"),sQuery(id+"F2.wireOp",EDGE,"E42"),sQuery(id+"F2.wireOp",EDGE,"E43"),sQuery(id+"F2.wireOp",EDGE,"E44"),sQuery(id+"F2.wireOp",EDGE,"E45")])],"isStart":true})]});
            var sketch = newSketch(context, id + "F32", { "sketchPlane" : qUnion([Q0])});
            skLineSegment(sketch, "E94", {"start": v(20.25, 40.5) * mm, "end": v(20.25, 0) * mm, "construction": true});
            skLineSegment(sketch, "E95", {"start": v(20.25, 20.25) * mm, "end": v(31.75, 20.25) * mm, "construction": true});
            skLineSegment(sketch, "E96", {"start": v(20.25, 20.25) * mm, "end": v(8.75, 20.25) * mm, "construction": true});
            skLineSegment(sketch, "E97", {"start": v(31.75, 22.75) * mm, "end": v(31.75, 17.75) * mm});
            skLineSegment(sketch, "E98", {"start": v(31.75, 17.75) * mm, "end": v(34.25, 17.75) * mm});
            skLineSegment(sketch, "E99", {"start": v(34.25, 17.75) * mm, "end": v(34.25, 22.75) * mm});
            skLineSegment(sketch, "E100", {"start": v(34.25, 22.75) * mm, "end": v(31.75, 22.75) * mm});
            skLineSegment(sketch, "E101.MirrorCS", {"start": v(8.75, 22.75) * mm, "end": v(8.75, 17.75) * mm});
            skLineSegment(sketch, "E102.MirrorCS", {"start": v(6.25, 22.75) * mm, "end": v(8.75, 22.75) * mm});
            skLineSegment(sketch, "E103.MirrorCS", {"start": v(6.25, 17.75) * mm, "end": v(6.25, 22.75) * mm});
            skLineSegment(sketch, "E104.MirrorCS", {"start": v(8.75, 17.75) * mm, "end": v(6.25, 17.75) * mm});
            skSolve(sketch);
        }
        {
            var Q0;
            {var subQ0=sQuery(id+"F0.wireOp",EDGE,"E0.top");var subQ1=sQuery(id+"F0.wireOp",EDGE,"E0.left");var subQ2=sQuery(id+"F0.wireOp",EDGE,"E6");var subQ3=sQuery(id+"F0.wireOp",EDGE,"E15");var subQ4=sQuery(id+"F0.wireOp",EDGE,"E18");var subQ5=sQuery(id+"F0.wireOp",EDGE,"E23.trimOffspring");var subQ6=sQuery(id+"F0.wireOp",EDGE,"E24.trimOffspring");var subQ7=sQuery(id+"F0.wireOp",EDGE,"E29");var subQ8=sQuery(id+"F0.wireOp",EDGE,"E30");Q0=makeQuery(id+"F3.boolean.opBoolean","SPLIT",FACE,{"disambiguationData":[TD([makeQuery(id+"F1.opExtrude","SWEPT_FACE",FACE,{"disambiguationData":[OSD([subQ2])]})])],"derivedFrom":makeQuery(id+"F1.opExtrude","CAP_FACE",FACE,{"disambiguationData":[OSD([subQ0,subQ1,sQuery(id+"F0.wireOp",EDGE,"E0.right"),subQ2,sQuery(id+"F0.wireOp",EDGE,"E10"),sQuery(id+"F0.wireOp",EDGE,"E11"),sQuery(id+"F0.wireOp",EDGE,"E12"),sQuery(id+"F0.wireOp",EDGE,"E16"),subQ3,subQ4,sQuery(id+"F0.wireOp",EDGE,"E17"),sQuery(id+"F0.wireOp",EDGE,"E22.trimOffspring"),subQ5,subQ6,sQuery(id+"F0.wireOp",EDGE,"E25.trimOffspring"),sQuery(id+"F0.wireOp",EDGE,"E27"),sQuery(id+"F0.wireOp",EDGE,"E28"),subQ7,subQ8,sQuery(id+"F0.wireOp",EDGE,"E31")])],"isStart":true})});}
            var sketch = newSketch(context, id + "F33", { "sketchPlane" : qUnion([Q0])});
            skArc(sketch, "E105", {"start": v(0, -37.57) * mm, "mid": v(0.86, -39.64) * mm, "end": v(2.93, -40.5) * mm});
            skCircle(sketch, "E106", {"center": v(2.93, -37.57) * mm, "radius": 1.75 * mm});
            skArc(sketch, "E107", {"start": v(8.17, -40.5) * mm, "mid": v(7.17, -33.33) * mm, "end": v(0, -32.33) * mm});
            skLineSegment(sketch, "E108", {"start": v(0, -37.57) * mm, "end": v(0, -32.33) * mm});
            skLineSegment(sketch, "E109", {"start": v(2.93, -40.5) * mm, "end": v(8.17, -40.5) * mm});
            skSolve(sketch);
        }
        {
            var Q0;
            Q0=qSketchRegion(id+"F33",true);
            extrude(context, id + "F34", {"entities" : qUnion([Q0]), "operationType" : NewBodyOperationType.ADD, "oppositeDirection" : true, "depth" : 5 * mm});
        }
        {
            var Q0;
            {var subQ0=sQuery(id+"F0.wireOp",EDGE,"E0.top");var subQ1=sQuery(id+"F0.wireOp",EDGE,"E0.left");var subQ2=sQuery(id+"F0.wireOp",EDGE,"E6");var subQ3=sQuery(id+"F0.wireOp",EDGE,"E15");var subQ4=sQuery(id+"F0.wireOp",EDGE,"E18");var subQ5=sQuery(id+"F0.wireOp",EDGE,"E23.trimOffspring");var subQ6=sQuery(id+"F0.wireOp",EDGE,"E24.trimOffspring");var subQ7=sQuery(id+"F0.wireOp",EDGE,"E29");var subQ8=sQuery(id+"F0.wireOp",EDGE,"E30");Q0=makeQuery(id+"F34.boolean.opBoolean","MERGE",FACE,{"derivedFrom":[makeQuery(id+"F3.boolean.opBoolean","SPLIT",FACE,{"disambiguationData":[TD([makeQuery(id+"F1.opExtrude","SWEPT_FACE",FACE,{"disambiguationData":[OSD([subQ2])]})])],"derivedFrom":makeQuery(id+"F1.opExtrude","CAP_FACE",FACE,{"disambiguationData":[OSD([subQ0,subQ1,sQuery(id+"F0.wireOp",EDGE,"E0.right"),subQ2,sQuery(id+"F0.wireOp",EDGE,"E10"),sQuery(id+"F0.wireOp",EDGE,"E11"),sQuery(id+"F0.wireOp",EDGE,"E12"),sQuery(id+"F0.wireOp",EDGE,"E16"),subQ3,subQ4,sQuery(id+"F0.wireOp",EDGE,"E17"),sQuery(id+"F0.wireOp",EDGE,"E22.trimOffspring"),subQ5,subQ6,sQuery(id+"F0.wireOp",EDGE,"E25.trimOffspring"),sQuery(id+"F0.wireOp",EDGE,"E27"),sQuery(id+"F0.wireOp",EDGE,"E28"),subQ7,subQ8,sQuery(id+"F0.wireOp",EDGE,"E31")])],"isStart":true})}),makeQuery(id+"F34.opExtrude","CAP_FACE",FACE,{"disambiguationData":[OSD([sQuery(id+"F33.wireOp",EDGE,"E105"),sQuery(id+"F33.wireOp",EDGE,"E106"),sQuery(id+"F33.wireOp",EDGE,"E107"),sQuery(id+"F33.wireOp",EDGE,"E108"),sQuery(id+"F33.wireOp",EDGE,"E109")])],"isStart":true})]});}
            var sketch = newSketch(context, id + "F35", { "sketchPlane" : qUnion([Q0])});
            skCircle(sketch, "E110", {"center": v(2.93, -37.57) * mm, "radius": 4.5 * mm});
            skSolve(sketch);
        }
        {
            var Q0;
            Q0=qSketchRegion(id+"F35",true);
            extrude(context, id + "F36", {"entities" : qUnion([Q0]), "operationType" : NewBodyOperationType.REMOVE, "oppositeDirection" : true, "depth" : 3.5 * mm});
        }
        {
            var Q0;
            {var subQ0=sQuery(id+"F0.wireOp",EDGE,"E0.top");var subQ1=sQuery(id+"F0.wireOp",EDGE,"E0.right");var subQ2=sQuery(id+"F0.wireOp",EDGE,"E10");var subQ3=sQuery(id+"F0.wireOp",EDGE,"E18");var subQ4=sQuery(id+"F0.wireOp",EDGE,"E17");var subQ5=sQuery(id+"F0.wireOp",EDGE,"E22.trimOffspring");var subQ6=sQuery(id+"F0.wireOp",EDGE,"E24.trimOffspring");var subQ7=sQuery(id+"F0.wireOp",EDGE,"E30");var subQ8=sQuery(id+"F0.wireOp",EDGE,"E31");Q0=makeQuery(id+"F3.boolean.opBoolean","SPLIT",FACE,{"disambiguationData":[TD([makeQuery(id+"F1.opExtrude","SWEPT_FACE",FACE,{"disambiguationData":[OSD([subQ2])]})])],"derivedFrom":makeQuery(id+"F1.opExtrude","CAP_FACE",FACE,{"disambiguationData":[OSD([subQ0,sQuery(id+"F0.wireOp",EDGE,"E0.left"),subQ1,sQuery(id+"F0.wireOp",EDGE,"E6"),subQ2,sQuery(id+"F0.wireOp",EDGE,"E11"),sQuery(id+"F0.wireOp",EDGE,"E12"),sQuery(id+"F0.wireOp",EDGE,"E16"),sQuery(id+"F0.wireOp",EDGE,"E15"),subQ3,subQ4,subQ5,sQuery(id+"F0.wireOp",EDGE,"E23.trimOffspring"),subQ6,sQuery(id+"F0.wireOp",EDGE,"E25.trimOffspring"),sQuery(id+"F0.wireOp",EDGE,"E27"),sQuery(id+"F0.wireOp",EDGE,"E28"),sQuery(id+"F0.wireOp",EDGE,"E29"),subQ7,subQ8])],"isStart":true})});}
            var sketch = newSketch(context, id + "F37", { "sketchPlane" : qUnion([Q0])});
            skCircle(sketch, "E111", {"center": v(37.57, -37.57) * mm, "radius": 1.75 * mm});
            skArc(sketch, "E112", {"start": v(37.57, -40.5) * mm, "mid": v(39.64, -39.64) * mm, "end": v(40.5, -37.57) * mm});
            skArc(sketch, "E113", {"start": v(40.5, -32.33) * mm, "mid": v(33.33, -33.33) * mm, "end": v(32.33, -40.5) * mm});
            skLineSegment(sketch, "E114", {"start": v(37.57, -40.5) * mm, "end": v(32.33, -40.5) * mm});
            skLineSegment(sketch, "E115", {"start": v(40.5, -32.33) * mm, "end": v(40.5, -37.57) * mm});
            skSolve(sketch);
        }
        {
            var Q0;
            Q0=qSketchRegion(id+"F37",true);
            extrude(context, id + "F38", {"entities" : qUnion([Q0]), "operationType" : NewBodyOperationType.ADD, "oppositeDirection" : true, "depth" : 5 * mm});
        }
        {
            var Q0;
            {var subQ0=sQuery(id+"F0.wireOp",EDGE,"E0.top");var subQ1=sQuery(id+"F0.wireOp",EDGE,"E0.right");var subQ2=sQuery(id+"F0.wireOp",EDGE,"E10");var subQ3=sQuery(id+"F0.wireOp",EDGE,"E18");var subQ4=sQuery(id+"F0.wireOp",EDGE,"E17");var subQ5=sQuery(id+"F0.wireOp",EDGE,"E22.trimOffspring");var subQ6=sQuery(id+"F0.wireOp",EDGE,"E24.trimOffspring");var subQ7=sQuery(id+"F0.wireOp",EDGE,"E30");var subQ8=sQuery(id+"F0.wireOp",EDGE,"E31");Q0=makeQuery(id+"F38.boolean.opBoolean","MERGE",FACE,{"derivedFrom":[makeQuery(id+"F3.boolean.opBoolean","SPLIT",FACE,{"disambiguationData":[TD([makeQuery(id+"F1.opExtrude","SWEPT_FACE",FACE,{"disambiguationData":[OSD([subQ2])]})])],"derivedFrom":makeQuery(id+"F1.opExtrude","CAP_FACE",FACE,{"disambiguationData":[OSD([subQ0,sQuery(id+"F0.wireOp",EDGE,"E0.left"),subQ1,sQuery(id+"F0.wireOp",EDGE,"E6"),subQ2,sQuery(id+"F0.wireOp",EDGE,"E11"),sQuery(id+"F0.wireOp",EDGE,"E12"),sQuery(id+"F0.wireOp",EDGE,"E16"),sQuery(id+"F0.wireOp",EDGE,"E15"),subQ3,subQ4,subQ5,sQuery(id+"F0.wireOp",EDGE,"E23.trimOffspring"),subQ6,sQuery(id+"F0.wireOp",EDGE,"E25.trimOffspring"),sQuery(id+"F0.wireOp",EDGE,"E27"),sQuery(id+"F0.wireOp",EDGE,"E28"),sQuery(id+"F0.wireOp",EDGE,"E29"),subQ7,subQ8])],"isStart":true})}),makeQuery(id+"F38.opExtrude","CAP_FACE",FACE,{"disambiguationData":[OSD([sQuery(id+"F37.wireOp",EDGE,"E111"),sQuery(id+"F37.wireOp",EDGE,"E112"),sQuery(id+"F37.wireOp",EDGE,"E113"),sQuery(id+"F37.wireOp",EDGE,"E114"),sQuery(id+"F37.wireOp",EDGE,"E115")])],"isStart":true})]});}
            var sketch = newSketch(context, id + "F39", { "sketchPlane" : qUnion([Q0])});
            skCircle(sketch, "E116", {"center": v(37.57, -37.57) * mm, "radius": 4.5 * mm});
            skSolve(sketch);
        }
        {
            var Q0;
            Q0=qSketchRegion(id+"F39",true);
            extrude(context, id + "F40", {"entities" : qUnion([Q0]), "operationType" : NewBodyOperationType.REMOVE, "oppositeDirection" : true, "depth" : 3.5 * mm});
        }
        {
            var Q0;
            {var subQ0=sQuery(id+"F0.wireOp",EDGE,"E0.right");var subQ1=sQuery(id+"F0.wireOp",EDGE,"E11");var subQ2=sQuery(id+"F0.wireOp",EDGE,"E16");var subQ3=sQuery(id+"F0.wireOp",EDGE,"E17");var subQ4=sQuery(id+"F0.wireOp",EDGE,"E22.trimOffspring");var subQ5=sQuery(id+"F0.wireOp",EDGE,"E25.trimOffspring");var subQ6=sQuery(id+"F0.wireOp",EDGE,"E27");var subQ7=sQuery(id+"F0.wireOp",EDGE,"E28");var subQ8=sQuery(id+"F0.wireOp",EDGE,"E31");Q0=makeQuery(id+"F3.boolean.opBoolean","SPLIT",FACE,{"disambiguationData":[TD([makeQuery(id+"F1.opExtrude","SWEPT_FACE",FACE,{"disambiguationData":[OSD([subQ1])]})])],"derivedFrom":makeQuery(id+"F1.opExtrude","CAP_FACE",FACE,{"disambiguationData":[OSD([sQuery(id+"F0.wireOp",EDGE,"E0.top"),sQuery(id+"F0.wireOp",EDGE,"E0.left"),subQ0,sQuery(id+"F0.wireOp",EDGE,"E6"),sQuery(id+"F0.wireOp",EDGE,"E10"),subQ1,sQuery(id+"F0.wireOp",EDGE,"E12"),subQ2,sQuery(id+"F0.wireOp",EDGE,"E15"),sQuery(id+"F0.wireOp",EDGE,"E18"),subQ3,subQ4,sQuery(id+"F0.wireOp",EDGE,"E23.trimOffspring"),sQuery(id+"F0.wireOp",EDGE,"E24.trimOffspring"),subQ5,subQ6,subQ7,sQuery(id+"F0.wireOp",EDGE,"E29"),sQuery(id+"F0.wireOp",EDGE,"E30"),subQ8])],"isStart":true})});}
            var sketch = newSketch(context, id + "F41", { "sketchPlane" : qUnion([Q0])});
            skCircle(sketch, "E117", {"center": v(37.57, -2.93) * mm, "radius": 1.75 * mm});
            skArc(sketch, "E118", {"start": v(40.5, -2.93) * mm, "mid": v(39.64, -0.86) * mm, "end": v(37.57, 0) * mm});
            skArc(sketch, "E119", {"start": v(32.33, 0) * mm, "mid": v(33.33, -7.17) * mm, "end": v(40.5, -8.17) * mm});
            skLineSegment(sketch, "E120", {"start": v(40.5, -2.93) * mm, "end": v(40.5, -8.17) * mm});
            skLineSegment(sketch, "E121", {"start": v(37.57, 0) * mm, "end": v(32.33, 0) * mm});
            skSolve(sketch);
        }
        {
            var Q0;
            Q0=qSketchRegion(id+"F41",true);
            extrude(context, id + "F42", {"entities" : qUnion([Q0]), "operationType" : NewBodyOperationType.ADD, "oppositeDirection" : true, "depth" : 5 * mm});
        }
        {
            var Q0;
            {var subQ0=sQuery(id+"F0.wireOp",EDGE,"E0.right");var subQ1=sQuery(id+"F0.wireOp",EDGE,"E11");var subQ2=sQuery(id+"F0.wireOp",EDGE,"E16");var subQ3=sQuery(id+"F0.wireOp",EDGE,"E17");var subQ4=sQuery(id+"F0.wireOp",EDGE,"E22.trimOffspring");var subQ5=sQuery(id+"F0.wireOp",EDGE,"E25.trimOffspring");var subQ6=sQuery(id+"F0.wireOp",EDGE,"E27");var subQ7=sQuery(id+"F0.wireOp",EDGE,"E28");var subQ8=sQuery(id+"F0.wireOp",EDGE,"E31");Q0=makeQuery(id+"F42.boolean.opBoolean","MERGE",FACE,{"derivedFrom":[makeQuery(id+"F3.boolean.opBoolean","SPLIT",FACE,{"disambiguationData":[TD([makeQuery(id+"F1.opExtrude","SWEPT_FACE",FACE,{"disambiguationData":[OSD([subQ1])]})])],"derivedFrom":makeQuery(id+"F1.opExtrude","CAP_FACE",FACE,{"disambiguationData":[OSD([sQuery(id+"F0.wireOp",EDGE,"E0.top"),sQuery(id+"F0.wireOp",EDGE,"E0.left"),subQ0,sQuery(id+"F0.wireOp",EDGE,"E6"),sQuery(id+"F0.wireOp",EDGE,"E10"),subQ1,sQuery(id+"F0.wireOp",EDGE,"E12"),subQ2,sQuery(id+"F0.wireOp",EDGE,"E15"),sQuery(id+"F0.wireOp",EDGE,"E18"),subQ3,subQ4,sQuery(id+"F0.wireOp",EDGE,"E23.trimOffspring"),sQuery(id+"F0.wireOp",EDGE,"E24.trimOffspring"),subQ5,subQ6,subQ7,sQuery(id+"F0.wireOp",EDGE,"E29"),sQuery(id+"F0.wireOp",EDGE,"E30"),subQ8])],"isStart":true})}),makeQuery(id+"F42.opExtrude","CAP_FACE",FACE,{"disambiguationData":[OSD([sQuery(id+"F41.wireOp",EDGE,"E117"),sQuery(id+"F41.wireOp",EDGE,"E118"),sQuery(id+"F41.wireOp",EDGE,"E119"),sQuery(id+"F41.wireOp",EDGE,"E120"),sQuery(id+"F41.wireOp",EDGE,"E121")])],"isStart":true})]});}
            var sketch = newSketch(context, id + "F43", { "sketchPlane" : qUnion([Q0])});
            skCircle(sketch, "E122", {"center": v(37.57, -2.93) * mm, "radius": 4.5 * mm});
            skSolve(sketch);
        }
        {
            var Q0;
            Q0=qSketchRegion(id+"F43",true);
            extrude(context, id + "F44", {"entities" : qUnion([Q0]), "operationType" : NewBodyOperationType.REMOVE, "oppositeDirection" : true, "depth" : 3.5 * mm});
        }
        {
            var Q0;
            {var subQ0=sQuery(id+"F0.wireOp",EDGE,"E0.left");var subQ1=sQuery(id+"F0.wireOp",EDGE,"E12");var subQ2=sQuery(id+"F0.wireOp",EDGE,"E16");var subQ3=sQuery(id+"F0.wireOp",EDGE,"E15");var subQ4=sQuery(id+"F0.wireOp",EDGE,"E23.trimOffspring");var subQ5=sQuery(id+"F0.wireOp",EDGE,"E25.trimOffspring");var subQ6=sQuery(id+"F0.wireOp",EDGE,"E27");var subQ7=sQuery(id+"F0.wireOp",EDGE,"E28");var subQ8=sQuery(id+"F0.wireOp",EDGE,"E29");Q0=makeQuery(id+"F3.boolean.opBoolean","SPLIT",FACE,{"disambiguationData":[TD([makeQuery(id+"F1.opExtrude","SWEPT_FACE",FACE,{"disambiguationData":[OSD([subQ1])]})])],"derivedFrom":makeQuery(id+"F1.opExtrude","CAP_FACE",FACE,{"disambiguationData":[OSD([sQuery(id+"F0.wireOp",EDGE,"E0.top"),subQ0,sQuery(id+"F0.wireOp",EDGE,"E0.right"),sQuery(id+"F0.wireOp",EDGE,"E6"),sQuery(id+"F0.wireOp",EDGE,"E10"),sQuery(id+"F0.wireOp",EDGE,"E11"),subQ1,subQ2,subQ3,sQuery(id+"F0.wireOp",EDGE,"E18"),sQuery(id+"F0.wireOp",EDGE,"E17"),sQuery(id+"F0.wireOp",EDGE,"E22.trimOffspring"),subQ4,sQuery(id+"F0.wireOp",EDGE,"E24.trimOffspring"),subQ5,subQ6,subQ7,subQ8,sQuery(id+"F0.wireOp",EDGE,"E30"),sQuery(id+"F0.wireOp",EDGE,"E31")])],"isStart":true})});}
            var sketch = newSketch(context, id + "F45", { "sketchPlane" : qUnion([Q0])});
            skCircle(sketch, "E123", {"center": v(2.93, -2.93) * mm, "radius": 1.75 * mm});
            skArc(sketch, "E124", {"start": v(2.93, 0) * mm, "mid": v(0.86, -0.86) * mm, "end": v(0, -2.93) * mm});
            skArc(sketch, "E125", {"start": v(0, -8.17) * mm, "mid": v(7.17, -7.17) * mm, "end": v(8.17, 0) * mm});
            skLineSegment(sketch, "E126", {"start": v(2.93, 0) * mm, "end": v(8.17, 0) * mm});
            skLineSegment(sketch, "E127", {"start": v(0, -2.93) * mm, "end": v(0, -8.17) * mm});
            skSolve(sketch);
        }
        {
            var Q0;
            Q0=qSketchRegion(id+"F45",true);
            extrude(context, id + "F46", {"entities" : qUnion([Q0]), "operationType" : NewBodyOperationType.ADD, "oppositeDirection" : true, "depth" : 5 * mm});
        }
        {
            var Q0;
            {var subQ0=sQuery(id+"F0.wireOp",EDGE,"E0.left");var subQ1=sQuery(id+"F0.wireOp",EDGE,"E12");var subQ2=sQuery(id+"F0.wireOp",EDGE,"E16");var subQ3=sQuery(id+"F0.wireOp",EDGE,"E15");var subQ4=sQuery(id+"F0.wireOp",EDGE,"E23.trimOffspring");var subQ5=sQuery(id+"F0.wireOp",EDGE,"E25.trimOffspring");var subQ6=sQuery(id+"F0.wireOp",EDGE,"E27");var subQ7=sQuery(id+"F0.wireOp",EDGE,"E28");var subQ8=sQuery(id+"F0.wireOp",EDGE,"E29");Q0=makeQuery(id+"F46.boolean.opBoolean","MERGE",FACE,{"derivedFrom":[makeQuery(id+"F3.boolean.opBoolean","SPLIT",FACE,{"disambiguationData":[TD([makeQuery(id+"F1.opExtrude","SWEPT_FACE",FACE,{"disambiguationData":[OSD([subQ1])]})])],"derivedFrom":makeQuery(id+"F1.opExtrude","CAP_FACE",FACE,{"disambiguationData":[OSD([sQuery(id+"F0.wireOp",EDGE,"E0.top"),subQ0,sQuery(id+"F0.wireOp",EDGE,"E0.right"),sQuery(id+"F0.wireOp",EDGE,"E6"),sQuery(id+"F0.wireOp",EDGE,"E10"),sQuery(id+"F0.wireOp",EDGE,"E11"),subQ1,subQ2,subQ3,sQuery(id+"F0.wireOp",EDGE,"E18"),sQuery(id+"F0.wireOp",EDGE,"E17"),sQuery(id+"F0.wireOp",EDGE,"E22.trimOffspring"),subQ4,sQuery(id+"F0.wireOp",EDGE,"E24.trimOffspring"),subQ5,subQ6,subQ7,subQ8,sQuery(id+"F0.wireOp",EDGE,"E30"),sQuery(id+"F0.wireOp",EDGE,"E31")])],"isStart":true})}),makeQuery(id+"F46.opExtrude","CAP_FACE",FACE,{"disambiguationData":[OSD([sQuery(id+"F45.wireOp",EDGE,"E123"),sQuery(id+"F45.wireOp",EDGE,"E124"),sQuery(id+"F45.wireOp",EDGE,"E125"),sQuery(id+"F45.wireOp",EDGE,"E126"),sQuery(id+"F45.wireOp",EDGE,"E127")])],"isStart":true})]});}
            var sketch = newSketch(context, id + "F47", { "sketchPlane" : qUnion([Q0])});
            skCircle(sketch, "E128", {"center": v(2.93, -2.93) * mm, "radius": 4.5 * mm});
            skSolve(sketch);
        }
        {
            var Q0;
            Q0=qSketchRegion(id+"F47",true);
            extrude(context, id + "F48", {"entities" : qUnion([Q0]), "operationType" : NewBodyOperationType.REMOVE, "oppositeDirection" : true, "depth" : 3.5 * mm});
        }
        {
            var Q0;
            {var subQ0=sQuery(id+"F0.wireOp",EDGE,"E0.top");var subQ1=sQuery(id+"F0.wireOp",EDGE,"E6");var subQ2=sQuery(id+"F0.wireOp",EDGE,"E10");var subQ3=sQuery(id+"F0.wireOp",EDGE,"E11");var subQ4=sQuery(id+"F0.wireOp",EDGE,"E12");var subQ5=sQuery(id+"F0.wireOp",EDGE,"E16");var subQ6=sQuery(id+"F0.wireOp",EDGE,"E15");var subQ7=sQuery(id+"F0.wireOp",EDGE,"E18");var subQ8=sQuery(id+"F0.wireOp",EDGE,"E17");var subQ9=sQuery(id+"F0.wireOp",EDGE,"E22.trimOffspring");var subQ10=sQuery(id+"F0.wireOp",EDGE,"E23.trimOffspring");var subQ11=sQuery(id+"F0.wireOp",EDGE,"E24.trimOffspring");var subQ12=sQuery(id+"F0.wireOp",EDGE,"E25.trimOffspring");var subQ13=sQuery(id+"F0.wireOp",EDGE,"E27");var subQ14=sQuery(id+"F0.wireOp",EDGE,"E28");var subQ15=sQuery(id+"F0.wireOp",EDGE,"E29");var subQ16=sQuery(id+"F0.wireOp",EDGE,"E30");var subQ17=sQuery(id+"F0.wireOp",EDGE,"E31");var subQ18=makeQuery(id+"F1.opExtrude","CAP_FACE",FACE,{"disambiguationData":[OSD([subQ0,sQuery(id+"F0.wireOp",EDGE,"E0.left"),sQuery(id+"F0.wireOp",EDGE,"E0.right"),subQ1,subQ2,subQ3,subQ4,subQ5,subQ6,subQ7,subQ8,subQ9,subQ10,subQ11,subQ12,subQ13,subQ14,subQ15,subQ16,subQ17])],"isStart":false});var subQ19=sQuery(id+"F2.wireOp",EDGE,"E34");var subQ20=sQuery(id+"F2.wireOp",EDGE,"E36");var subQ21=sQuery(id+"F2.wireOp",EDGE,"E38");var subQ22=sQuery(id+"F2.wireOp",EDGE,"E39");var subQ23=sQuery(id+"F2.wireOp",EDGE,"E40");var subQ24=sQuery(id+"F2.wireOp",EDGE,"E41");var subQ25=sQuery(id+"F2.wireOp",EDGE,"E42");var subQ26=sQuery(id+"F2.wireOp",EDGE,"E43");var subQ27=sQuery(id+"F2.wireOp",EDGE,"E44");var subQ28=sQuery(id+"F2.wireOp",EDGE,"E45");var subQ29=makeQuery(id+"F3.opExtrude","CAP_FACE",FACE,{"disambiguationData":[OSD([subQ19,sQuery(id+"F2.wireOp",EDGE,"E35"),subQ20,sQuery(id+"F2.wireOp",EDGE,"E37"),subQ21,subQ22,subQ23,subQ24,subQ25,subQ26,subQ27,subQ28])],"isStart":true});Q0=makeQuery(id+"FTp76k74SmvxBSS_1.boolean.opBoolean","SPLIT",FACE,{"disambiguationData":[TD([makeQuery(id+"F1.opExtrude","SWEPT_FACE",FACE,{"disambiguationData":[OSD([subQ0])]})])],"derivedFrom":makeQuery(id+"F3.boolean.opBoolean","MERGE",FACE,{"derivedFrom":[subQ18,subQ29]})});}
            var sketch = newSketch(context, id + "F49", { "sketchPlane" : qUnion([Q0])});
            skLineSegment(sketch, "E129", {"start": v(31.75, 20.25) * mm, "end": v(8.75, 20.25) * mm, "construction": true});
            skLineSegment(sketch, "E130", {"start": v(8.75, 21.5) * mm, "end": v(8.75, 19) * mm});
            skLineSegment(sketch, "E131", {"start": v(20.25, 40.5) * mm, "end": v(20.25, 0) * mm, "construction": true});
            skLineSegment(sketch, "E132", {"start": v(8.75, 21.5) * mm, "end": v(10.75, 21.5) * mm});
            skLineSegment(sketch, "E133", {"start": v(10.75, 21.5) * mm, "end": v(10.75, 19) * mm});
            skLineSegment(sketch, "E134", {"start": v(10.75, 19) * mm, "end": v(8.75, 19) * mm});
            skLineSegment(sketch, "E135.MirrorCS", {"start": v(31.75, 21.5) * mm, "end": v(31.75, 19) * mm});
            skLineSegment(sketch, "E136.MirrorCS", {"start": v(29.75, 21.5) * mm, "end": v(29.75, 19) * mm});
            skLineSegment(sketch, "E137.MirrorCS", {"start": v(31.75, 21.5) * mm, "end": v(29.75, 21.5) * mm});
            skLineSegment(sketch, "E138.MirrorCS", {"start": v(29.75, 19) * mm, "end": v(31.75, 19) * mm});
            skSolve(sketch);
        }
        {
            var Q0;
            Q0=makeQuery(id+"F13.boolean.opBoolean","COPY",FACE,{"derivedFrom":makeQuery(id+"F13.opExtrude","CAP_FACE",FACE,{"disambiguationData":[OSD([sQuery(id+"F12.wireOp",EDGE,"E59"),sQuery(id+"F12.wireOp",EDGE,"E61"),sQuery(id+"F12.wireOp",EDGE,"E63"),sQuery(id+"F12.wireOp",EDGE,"E65"),sQuery(id+"F12.wireOp",EDGE,"E66"),sQuery(id+"F12.wireOp",EDGE,"E67"),sQuery(id+"F12.wireOp",EDGE,"E68"),sQuery(id+"F12.wireOp",EDGE,"E69"),sQuery(id+"F12.wireOp",EDGE,"E70"),sQuery(id+"F12.wireOp",EDGE,"E71"),sQuery(id+"F12.wireOp",EDGE,"E72"),sQuery(id+"F12.wireOp",EDGE,"E73")])],"isStart":false})});
            var sketch = newSketch(context, id + "F50", { "sketchPlane" : qUnion([Q0])});
            skLineSegment(sketch, "E139.bottom", {"start": v(22.75, -17.75) * mm, "end": v(17.75, -17.75) * mm, "construction": true});
            skLineSegment(sketch, "E139.top", {"start": v(22.75, -22.75) * mm, "end": v(17.75, -22.75) * mm, "construction": true});
            skLineSegment(sketch, "E139.left", {"start": v(22.75, -17.75) * mm, "end": v(22.75, -22.75) * mm, "construction": true});
            skLineSegment(sketch, "E139.right", {"start": v(17.75, -17.75) * mm, "end": v(17.75, -22.75) * mm, "construction": true});
            skLineSegment(sketch, "E140", {"start": v(17.75, -22.75) * mm, "end": v(17.75, -32.5) * mm});
            skLineSegment(sketch, "E141", {"start": v(17.75, -32.5) * mm, "end": v(19, -32.5) * mm});
            skLineSegment(sketch, "E142", {"start": v(22.75, -32.5) * mm, "end": v(22.75, -22.75) * mm});
            skLineSegment(sketch, "E143", {"start": v(22.75, -22.75) * mm, "end": v(32.5, -22.75) * mm});
            skLineSegment(sketch, "E144", {"start": v(32.5, -22.75) * mm, "end": v(32.5, -21.5) * mm});
            skLineSegment(sketch, "E145", {"start": v(32.5, -17.75) * mm, "end": v(22.75, -17.75) * mm});
            skLineSegment(sketch, "E146", {"start": v(22.75, -17.75) * mm, "end": v(22.75, -8) * mm});
            skLineSegment(sketch, "E147", {"start": v(22.75, -8) * mm, "end": v(21.5, -8) * mm});
            skLineSegment(sketch, "E148", {"start": v(17.75, -8) * mm, "end": v(17.75, -17.75) * mm});
            skLineSegment(sketch, "E149", {"start": v(17.75, -17.75) * mm, "end": v(8, -17.75) * mm});
            skLineSegment(sketch, "E150", {"start": v(8, -17.75) * mm, "end": v(8, -19) * mm});
            skLineSegment(sketch, "E151", {"start": v(8, -22.75) * mm, "end": v(17.75, -22.75) * mm});
            skLineSegment(sketch, "E152", {"start": v(17.75, -17.75) * mm, "end": v(22.75, -22.75) * mm, "construction": true});
            skLineSegment(sketch, "E153.rect.bottom", {"start": v(19, -21.5) * mm, "end": v(21.5, -21.5) * mm, "construction": true});
            skLineSegment(sketch, "E153.rect.top", {"start": v(19, -19) * mm, "end": v(21.5, -19) * mm, "construction": true});
            skLineSegment(sketch, "E153.rect.left", {"start": v(19, -21.5) * mm, "end": v(19, -19) * mm, "construction": true});
            skLineSegment(sketch, "E153.rect.right", {"start": v(21.5, -21.5) * mm, "end": v(21.5, -19) * mm, "construction": true});
            skPoint(sketch, "E153.rect.middle", {"position": v(20.25, -20.25) * mm});
            skLineSegment(sketch, "E154", {"start": v(19, -21.5) * mm, "end": v(19, -32.5) * mm});
            skLineSegment(sketch, "E155", {"start": v(21.5, -21.5) * mm, "end": v(21.5, -32.5) * mm});
            skLineSegment(sketch, "E156", {"start": v(19, -21.5) * mm, "end": v(8, -21.5) * mm});
            skLineSegment(sketch, "E157", {"start": v(19, -19) * mm, "end": v(8, -19) * mm});
            skLineSegment(sketch, "E158", {"start": v(19, -19) * mm, "end": v(19, -8) * mm});
            skLineSegment(sketch, "E159", {"start": v(21.5, -19) * mm, "end": v(21.5, -8) * mm});
            skLineSegment(sketch, "E160", {"start": v(21.5, -19) * mm, "end": v(32.5, -19) * mm});
            skLineSegment(sketch, "E161", {"start": v(21.5, -21.5) * mm, "end": v(32.5, -21.5) * mm});
            skLineSegment(sketch, "E162", {"start": v(19, -32.5) * mm, "end": v(21.5, -32.5) * mm, "construction": true});
            skLineSegment(sketch, "E163", {"start": v(21.5, -32.5) * mm, "end": v(22.75, -32.5) * mm});
            skLineSegment(sketch, "E164", {"start": v(8, -21.5) * mm, "end": v(8, -21.5) * mm});
            skLineSegment(sketch, "E165", {"start": v(8, -19) * mm, "end": v(8, -19) * mm});
            skLineSegment(sketch, "E166", {"start": v(19, -8) * mm, "end": v(17.75, -8) * mm});
            skLineSegment(sketch, "E167", {"start": v(21.5, -8) * mm, "end": v(19, -8) * mm, "construction": true});
            skLineSegment(sketch, "E168", {"start": v(32.5, -21.5) * mm, "end": v(32.5, -19) * mm, "construction": true});
            skLineSegment(sketch, "E169", {"start": v(32.5, -19) * mm, "end": v(32.5, -17.75) * mm});
            skLineSegment(sketch, "E170", {"start": v(8, -21.5) * mm, "end": v(8, -22.75) * mm});
            skLineSegment(sketch, "E171", {"start": v(8, -19) * mm, "end": v(8, -21.5) * mm, "construction": true});
            skSolve(sketch);
        }
        {
            var Q0;
            Q0 = qSketchRegion(id + "F50", true);
            extrude(context, id + "F51", {"entities" : qUnion([Q0]), "operationType" : NewBodyOperationType.REMOVE, "oppositeDirection" : true, "depth" : 25 * mm});
        }
        {
            var Q0;
            Q0=makeQuery(id+"F17.opExtrude","CAP_EDGE",EDGE,{"disambiguationData":[OSD([sQuery(id+"F16.wireOp",EDGE,"E80")])],"isStart":true});
            var Q1;
            Q1=makeQuery(id+"F23.opExtrude","CAP_EDGE",EDGE,{"disambiguationData":[OSD([sQuery(id+"F22.wireOp",EDGE,"E89")])],"isStart":true});
            var Q2;
            Q2=makeQuery(id+"F21.opExtrude","CAP_EDGE",EDGE,{"disambiguationData":[OSD([sQuery(id+"F20.wireOp",EDGE,"E86")])],"isStart":true});
            var Q3;
            Q3=makeQuery(id+"F19.opExtrude","CAP_EDGE",EDGE,{"disambiguationData":[OSD([sQuery(id+"F18.wireOp",EDGE,"E83")])],"isStart":true});
            var Q4;
            Q4=makeQuery(id+"F48.boolean.opBoolean","COPY",EDGE,{"derivedFrom":makeQuery(id+"F48.opExtrude","CAP_EDGE",EDGE,{"disambiguationData":[OSD([sQuery(id+"F47.wireOp",EDGE,"E128")])],"isStart":false})});
            var Q5;
            Q5=makeQuery(id+"F44.boolean.opBoolean","COPY",EDGE,{"derivedFrom":makeQuery(id+"F44.opExtrude","CAP_EDGE",EDGE,{"disambiguationData":[OSD([sQuery(id+"F43.wireOp",EDGE,"E122")])],"isStart":false})});
            var Q6;
            Q6=makeQuery(id+"F40.boolean.opBoolean","COPY",EDGE,{"derivedFrom":makeQuery(id+"F40.opExtrude","CAP_EDGE",EDGE,{"disambiguationData":[OSD([sQuery(id+"F39.wireOp",EDGE,"E116")])],"isStart":false})});
            var Q7;
            Q7=makeQuery(id+"F36.boolean.opBoolean","COPY",EDGE,{"derivedFrom":makeQuery(id+"F36.opExtrude","CAP_EDGE",EDGE,{"disambiguationData":[OSD([sQuery(id+"F35.wireOp",EDGE,"E110")])],"isStart":false})});
            var Q8;
            Q8=makeQuery(id+"F46.boolean.opBoolean","INTERSECT",EDGE,{"derivedFrom":[makeQuery(id+"F15.boolean.opBoolean","MERGE",FACE,{"derivedFrom":[makeQuery(id+"F1.opExtrude","SWEPT_FACE",FACE,{"disambiguationData":[OSD([sQuery(id+"F0.wireOp",EDGE,"E12")])]}),makeQuery(id+"F15.opExtrude","SWEPT_FACE",FACE,{"disambiguationData":[OSD([sQuery(id+"F14.wireOp",EDGE,"E76")])]})]}),makeQuery(id+"F46.opExtrude","CAP_FACE",FACE,{"disambiguationData":[OSD([sQuery(id+"F45.wireOp",EDGE,"E123"),sQuery(id+"F45.wireOp",EDGE,"E124"),sQuery(id+"F45.wireOp",EDGE,"E125"),sQuery(id+"F45.wireOp",EDGE,"E126"),sQuery(id+"F45.wireOp",EDGE,"E127")])],"isStart":false})]});
            var Q9;
            Q9=makeQuery(id+"F34.boolean.opBoolean","INTERSECT",EDGE,{"derivedFrom":[makeQuery(id+"F15.boolean.opBoolean","MERGE",FACE,{"derivedFrom":[makeQuery(id+"F1.opExtrude","SWEPT_FACE",FACE,{"disambiguationData":[OSD([sQuery(id+"F0.wireOp",EDGE,"E6")])]}),makeQuery(id+"F15.opExtrude","SWEPT_FACE",FACE,{"disambiguationData":[OSD([sQuery(id+"F14.wireOp",EDGE,"E77")])]})]}),makeQuery(id+"F34.opExtrude","CAP_FACE",FACE,{"disambiguationData":[OSD([sQuery(id+"F33.wireOp",EDGE,"E105"),sQuery(id+"F33.wireOp",EDGE,"E106"),sQuery(id+"F33.wireOp",EDGE,"E107"),sQuery(id+"F33.wireOp",EDGE,"E108"),sQuery(id+"F33.wireOp",EDGE,"E109")])],"isStart":false})]});
            var Q10;
            Q10=makeQuery(id+"F38.boolean.opBoolean","INTERSECT",EDGE,{"derivedFrom":[makeQuery(id+"F15.boolean.opBoolean","MERGE",FACE,{"derivedFrom":[makeQuery(id+"F1.opExtrude","SWEPT_FACE",FACE,{"disambiguationData":[OSD([sQuery(id+"F0.wireOp",EDGE,"E10")])]}),makeQuery(id+"F15.opExtrude","SWEPT_FACE",FACE,{"disambiguationData":[OSD([sQuery(id+"F14.wireOp",EDGE,"E74")])]})]}),makeQuery(id+"F38.opExtrude","CAP_FACE",FACE,{"disambiguationData":[OSD([sQuery(id+"F37.wireOp",EDGE,"E111"),sQuery(id+"F37.wireOp",EDGE,"E112"),sQuery(id+"F37.wireOp",EDGE,"E113"),sQuery(id+"F37.wireOp",EDGE,"E114"),sQuery(id+"F37.wireOp",EDGE,"E115")])],"isStart":false})]});
            var Q11;
            Q11=makeQuery(id+"F42.boolean.opBoolean","INTERSECT",EDGE,{"derivedFrom":[makeQuery(id+"F15.boolean.opBoolean","MERGE",FACE,{"derivedFrom":[makeQuery(id+"F1.opExtrude","SWEPT_FACE",FACE,{"disambiguationData":[OSD([sQuery(id+"F0.wireOp",EDGE,"E11")])]}),makeQuery(id+"F15.opExtrude","SWEPT_FACE",FACE,{"disambiguationData":[OSD([sQuery(id+"F14.wireOp",EDGE,"E75")])]})]}),makeQuery(id+"F42.opExtrude","CAP_FACE",FACE,{"disambiguationData":[OSD([sQuery(id+"F41.wireOp",EDGE,"E117"),sQuery(id+"F41.wireOp",EDGE,"E118"),sQuery(id+"F41.wireOp",EDGE,"E119"),sQuery(id+"F41.wireOp",EDGE,"E120"),sQuery(id+"F41.wireOp",EDGE,"E121")])],"isStart":false})]});
            var Q12;
            {var subQ0=sQuery(id+"F12.wireOp",EDGE,"E61");var subQ1=sQuery(id+"F50.wireOp",EDGE,"E154");var subQ2=sQuery(id+"F50.wireOp",EDGE,"E141");Q12=makeQuery(id+"F51.boolean.opBoolean","COPY",EDGE,{"disambiguationData":[topologyDisambiguationEdgeConnected([makeQuery(id+"F13.boolean.opBoolean","COPY",FACE,{"derivedFrom":makeQuery(id+"F13.opExtrude","SWEPT_FACE",FACE,{"disambiguationData":[OSD([subQ0])]})})])],"derivedFrom":makeQuery(id+"F51.opExtrude","SWEPT_EDGE",EDGE,{"disambiguationData":[OSD([subQ0,subQ2,subQ1])]})});}
            var Q13;
            {var subQ0=sQuery(id+"F12.wireOp",EDGE,"E61");var subQ1=sQuery(id+"F50.wireOp",EDGE,"E163");var subQ2=sQuery(id+"F50.wireOp",EDGE,"E155");Q13=makeQuery(id+"F51.boolean.opBoolean","COPY",EDGE,{"disambiguationData":[topologyDisambiguationEdgeConnected([makeQuery(id+"F13.boolean.opBoolean","COPY",FACE,{"derivedFrom":makeQuery(id+"F13.opExtrude","SWEPT_FACE",FACE,{"disambiguationData":[OSD([subQ0])]})})])],"derivedFrom":makeQuery(id+"F51.opExtrude","SWEPT_EDGE",EDGE,{"disambiguationData":[OSD([subQ0,subQ2,subQ1])]})});}
            var Q14;
            {var subQ4=sQuery(id+"F0.wireOp",EDGE,"E30");var subQ8=sQuery(id+"F0.wireOp",EDGE,"E24.trimOffspring");var subQ11=sQuery(id+"F0.wireOp",EDGE,"E18");var subQ20=sQuery(id+"F2.wireOp",EDGE,"E43");Q14=makeQuery(id+"F34.boolean.opBoolean","INTERSECT",EDGE,{"derivedFrom":[makeQuery(id+"F3.boolean.opBoolean","SPLIT",FACE,{"disambiguationData":[TD([makeQuery(id+"F3.opExtrude","SWEPT_FACE",FACE,{"disambiguationData":[OSD([subQ20])]})])],"derivedFrom":makeQuery(id+"F1.opExtrude","SWEPT_FACE",FACE,{"disambiguationData":[OSD([subQ11,subQ8,subQ4])]})}),makeQuery(id+"F34.opExtrude","SWEPT_FACE",FACE,{"disambiguationData":[OSD([sQuery(id+"F33.wireOp",EDGE,"E107")])]})]});}
            var Q15;
            {var subQ4=sQuery(id+"F0.wireOp",EDGE,"E29");var subQ8=sQuery(id+"F0.wireOp",EDGE,"E23.trimOffspring");var subQ11=sQuery(id+"F0.wireOp",EDGE,"E15");var subQ20=sQuery(id+"F2.wireOp",EDGE,"E42");Q15=makeQuery(id+"F34.boolean.opBoolean","INTERSECT",EDGE,{"derivedFrom":[makeQuery(id+"F3.boolean.opBoolean","SPLIT",FACE,{"disambiguationData":[TD([makeQuery(id+"F3.opExtrude","SWEPT_FACE",FACE,{"disambiguationData":[OSD([subQ20])]})])],"derivedFrom":makeQuery(id+"F1.opExtrude","SWEPT_FACE",FACE,{"disambiguationData":[OSD([subQ11,subQ8,subQ4])]})}),makeQuery(id+"F34.opExtrude","SWEPT_FACE",FACE,{"disambiguationData":[OSD([sQuery(id+"F33.wireOp",EDGE,"E107")])]})]});}
            var Q16;
            Q16=makeQuery(id+"F3.boolean.opBoolean","INTERSECT",EDGE,{"derivedFrom":[makeQuery(id+"F1.opExtrude","SWEPT_FACE",FACE,{"disambiguationData":[OSD([sQuery(id+"F0.wireOp",EDGE,"E15"),sQuery(id+"F0.wireOp",EDGE,"E23.trimOffspring"),sQuery(id+"F0.wireOp",EDGE,"E29")])]}),makeQuery(id+"F3.opExtrude","SWEPT_FACE",FACE,{"disambiguationData":[OSD([sQuery(id+"F2.wireOp",EDGE,"E42")])]})]});
            var Q17;
            {var subQ0=sQuery(id+"F12.wireOp",EDGE,"E59");var subQ1=sQuery(id+"F50.wireOp",EDGE,"E156");var subQ2=sQuery(id+"F50.wireOp",EDGE,"E170");Q17=makeQuery(id+"F51.boolean.opBoolean","COPY",EDGE,{"disambiguationData":[topologyDisambiguationEdgeConnected([makeQuery(id+"F13.boolean.opBoolean","COPY",FACE,{"derivedFrom":makeQuery(id+"F13.opExtrude","SWEPT_FACE",FACE,{"disambiguationData":[OSD([subQ0])]})})])],"derivedFrom":makeQuery(id+"F51.opExtrude","SWEPT_EDGE",EDGE,{"disambiguationData":[OSD([subQ0,subQ1,subQ2])]})});}
            var Q18;
            {var subQ0=sQuery(id+"F12.wireOp",EDGE,"E59");var subQ1=sQuery(id+"F50.wireOp",EDGE,"E150");var subQ2=sQuery(id+"F50.wireOp",EDGE,"E157");Q18=makeQuery(id+"F51.boolean.opBoolean","COPY",EDGE,{"disambiguationData":[topologyDisambiguationEdgeConnected([makeQuery(id+"F13.boolean.opBoolean","COPY",FACE,{"derivedFrom":makeQuery(id+"F13.opExtrude","SWEPT_FACE",FACE,{"disambiguationData":[OSD([subQ0])]})})])],"derivedFrom":makeQuery(id+"F51.opExtrude","SWEPT_EDGE",EDGE,{"disambiguationData":[OSD([subQ0,subQ1,subQ2])]})});}
            var Q19;
            Q19=makeQuery(id+"F3.boolean.opBoolean","INTERSECT",EDGE,{"derivedFrom":[makeQuery(id+"F1.opExtrude","SWEPT_FACE",FACE,{"disambiguationData":[OSD([sQuery(id+"F0.wireOp",EDGE,"E15"),sQuery(id+"F0.wireOp",EDGE,"E23.trimOffspring"),sQuery(id+"F0.wireOp",EDGE,"E29")])]}),makeQuery(id+"F3.opExtrude","SWEPT_FACE",FACE,{"disambiguationData":[OSD([sQuery(id+"F2.wireOp",EDGE,"E41")])]})]});
            var Q20;
            Q20=makeQuery(id+"F3.boolean.opBoolean","INTERSECT",EDGE,{"derivedFrom":[makeQuery(id+"F1.opExtrude","SWEPT_FACE",FACE,{"disambiguationData":[OSD([sQuery(id+"F0.wireOp",EDGE,"E18"),sQuery(id+"F0.wireOp",EDGE,"E24.trimOffspring"),sQuery(id+"F0.wireOp",EDGE,"E30")])]}),makeQuery(id+"F3.opExtrude","SWEPT_FACE",FACE,{"disambiguationData":[OSD([sQuery(id+"F2.wireOp",EDGE,"E44")])]})]});
            var Q21;
            Q21=makeQuery(id+"F3.boolean.opBoolean","INTERSECT",EDGE,{"derivedFrom":[makeQuery(id+"F1.opExtrude","SWEPT_FACE",FACE,{"disambiguationData":[OSD([sQuery(id+"F0.wireOp",EDGE,"E18"),sQuery(id+"F0.wireOp",EDGE,"E24.trimOffspring"),sQuery(id+"F0.wireOp",EDGE,"E30")])]}),makeQuery(id+"F3.opExtrude","SWEPT_FACE",FACE,{"disambiguationData":[OSD([sQuery(id+"F2.wireOp",EDGE,"E43")])]})]});
            var Q22;
            {var subQ3=sQuery(id+"F0.wireOp",EDGE,"E30");var subQ8=sQuery(id+"F0.wireOp",EDGE,"E24.trimOffspring");var subQ10=sQuery(id+"F0.wireOp",EDGE,"E18");var subQ20=sQuery(id+"F2.wireOp",EDGE,"E44");Q22=makeQuery(id+"F38.boolean.opBoolean","INTERSECT",EDGE,{"derivedFrom":[makeQuery(id+"F3.boolean.opBoolean","SPLIT",FACE,{"disambiguationData":[TD([makeQuery(id+"F3.opExtrude","SWEPT_FACE",FACE,{"disambiguationData":[OSD([subQ20])]})])],"derivedFrom":makeQuery(id+"F1.opExtrude","SWEPT_FACE",FACE,{"disambiguationData":[OSD([subQ10,subQ8,subQ3])]})}),makeQuery(id+"F38.opExtrude","SWEPT_FACE",FACE,{"disambiguationData":[OSD([sQuery(id+"F37.wireOp",EDGE,"E113")])]})]});}
            var Q23;
            {var subQ3=sQuery(id+"F0.wireOp",EDGE,"E31");var subQ9=sQuery(id+"F0.wireOp",EDGE,"E22.trimOffspring");var subQ10=sQuery(id+"F0.wireOp",EDGE,"E17");var subQ20=sQuery(id+"F2.wireOp",EDGE,"E45");Q23=makeQuery(id+"F38.boolean.opBoolean","INTERSECT",EDGE,{"derivedFrom":[makeQuery(id+"F3.boolean.opBoolean","SPLIT",FACE,{"disambiguationData":[TD([makeQuery(id+"F3.opExtrude","SWEPT_FACE",FACE,{"disambiguationData":[OSD([subQ20])]})])],"derivedFrom":makeQuery(id+"F1.opExtrude","SWEPT_FACE",FACE,{"disambiguationData":[OSD([subQ10,subQ9,subQ3])]})}),makeQuery(id+"F38.opExtrude","SWEPT_FACE",FACE,{"disambiguationData":[OSD([sQuery(id+"F37.wireOp",EDGE,"E113")])]})]});}
            var Q24;
            Q24=makeQuery(id+"F3.boolean.opBoolean","INTERSECT",EDGE,{"derivedFrom":[makeQuery(id+"F1.opExtrude","SWEPT_FACE",FACE,{"disambiguationData":[OSD([sQuery(id+"F0.wireOp",EDGE,"E17"),sQuery(id+"F0.wireOp",EDGE,"E22.trimOffspring"),sQuery(id+"F0.wireOp",EDGE,"E31")])]}),makeQuery(id+"F3.opExtrude","SWEPT_FACE",FACE,{"disambiguationData":[OSD([sQuery(id+"F2.wireOp",EDGE,"E38")])]})]});
            var Q25;
            {var subQ0=sQuery(id+"F12.wireOp",EDGE,"E63");var subQ1=sQuery(id+"F50.wireOp",EDGE,"E160");var subQ2=sQuery(id+"F50.wireOp",EDGE,"E169");Q25=makeQuery(id+"F51.boolean.opBoolean","COPY",EDGE,{"disambiguationData":[topologyDisambiguationEdgeConnected([makeQuery(id+"F13.boolean.opBoolean","COPY",FACE,{"derivedFrom":makeQuery(id+"F13.opExtrude","SWEPT_FACE",FACE,{"disambiguationData":[OSD([subQ0])]})})])],"derivedFrom":makeQuery(id+"F51.opExtrude","SWEPT_EDGE",EDGE,{"disambiguationData":[OSD([subQ0,subQ1,subQ2])]})});}
            var Q26;
            {var subQ0=sQuery(id+"F12.wireOp",EDGE,"E63");var subQ1=sQuery(id+"F50.wireOp",EDGE,"E144");var subQ2=sQuery(id+"F50.wireOp",EDGE,"E161");Q26=makeQuery(id+"F51.boolean.opBoolean","COPY",EDGE,{"disambiguationData":[topologyDisambiguationEdgeConnected([makeQuery(id+"F13.boolean.opBoolean","COPY",FACE,{"derivedFrom":makeQuery(id+"F13.opExtrude","SWEPT_FACE",FACE,{"disambiguationData":[OSD([subQ0])]})})])],"derivedFrom":makeQuery(id+"F51.opExtrude","SWEPT_EDGE",EDGE,{"disambiguationData":[OSD([subQ0,subQ1,subQ2])]})});}
            var Q27;
            Q27=makeQuery(id+"F3.boolean.opBoolean","INTERSECT",EDGE,{"derivedFrom":[makeQuery(id+"F1.opExtrude","SWEPT_FACE",FACE,{"disambiguationData":[OSD([sQuery(id+"F0.wireOp",EDGE,"E17"),sQuery(id+"F0.wireOp",EDGE,"E22.trimOffspring"),sQuery(id+"F0.wireOp",EDGE,"E31")])]}),makeQuery(id+"F3.opExtrude","SWEPT_FACE",FACE,{"disambiguationData":[OSD([sQuery(id+"F2.wireOp",EDGE,"E45")])]})]});
            var Q28;
            {var subQ3=sQuery(id+"F0.wireOp",EDGE,"E31");var subQ9=sQuery(id+"F0.wireOp",EDGE,"E22.trimOffspring");var subQ10=sQuery(id+"F0.wireOp",EDGE,"E17");var subQ20=sQuery(id+"F2.wireOp",EDGE,"E38");Q28=makeQuery(id+"F42.boolean.opBoolean","INTERSECT",EDGE,{"derivedFrom":[makeQuery(id+"F3.boolean.opBoolean","SPLIT",FACE,{"disambiguationData":[TD([makeQuery(id+"F3.opExtrude","SWEPT_FACE",FACE,{"disambiguationData":[OSD([subQ20])]})])],"derivedFrom":makeQuery(id+"F1.opExtrude","SWEPT_FACE",FACE,{"disambiguationData":[OSD([subQ10,subQ9,subQ3])]})}),makeQuery(id+"F42.opExtrude","SWEPT_FACE",FACE,{"disambiguationData":[OSD([sQuery(id+"F41.wireOp",EDGE,"E119")])]})]});}
            var Q29;
            {var subQ5=sQuery(id+"F0.wireOp",EDGE,"E28");var subQ7=sQuery(id+"F0.wireOp",EDGE,"E25.trimOffspring");var subQ12=sQuery(id+"F0.wireOp",EDGE,"E16");var subQ20=sQuery(id+"F2.wireOp",EDGE,"E39");Q29=makeQuery(id+"F42.boolean.opBoolean","INTERSECT",EDGE,{"derivedFrom":[makeQuery(id+"F3.boolean.opBoolean","SPLIT",FACE,{"disambiguationData":[TD([makeQuery(id+"F3.opExtrude","SWEPT_FACE",FACE,{"disambiguationData":[OSD([subQ20])]})])],"derivedFrom":makeQuery(id+"F1.opExtrude","SWEPT_FACE",FACE,{"disambiguationData":[OSD([subQ12,subQ7,subQ5])]})}),makeQuery(id+"F42.opExtrude","SWEPT_FACE",FACE,{"disambiguationData":[OSD([sQuery(id+"F41.wireOp",EDGE,"E119")])]})]});}
            var Q30;
            Q30=makeQuery(id+"F3.boolean.opBoolean","INTERSECT",EDGE,{"derivedFrom":[makeQuery(id+"F1.opExtrude","SWEPT_FACE",FACE,{"disambiguationData":[OSD([sQuery(id+"F0.wireOp",EDGE,"E16"),sQuery(id+"F0.wireOp",EDGE,"E25.trimOffspring"),sQuery(id+"F0.wireOp",EDGE,"E28")])]}),makeQuery(id+"F3.opExtrude","SWEPT_FACE",FACE,{"disambiguationData":[OSD([sQuery(id+"F2.wireOp",EDGE,"E39")])]})]});
            var Q31;
            {var subQ0=sQuery(id+"F12.wireOp",EDGE,"E65");var subQ1=sQuery(id+"F50.wireOp",EDGE,"E147");var subQ2=sQuery(id+"F50.wireOp",EDGE,"E159");Q31=makeQuery(id+"F51.boolean.opBoolean","COPY",EDGE,{"disambiguationData":[topologyDisambiguationEdgeConnected([makeQuery(id+"F13.boolean.opBoolean","COPY",FACE,{"derivedFrom":makeQuery(id+"F13.opExtrude","SWEPT_FACE",FACE,{"disambiguationData":[OSD([subQ0])]})})])],"derivedFrom":makeQuery(id+"F51.opExtrude","SWEPT_EDGE",EDGE,{"disambiguationData":[OSD([subQ0,subQ1,subQ2])]})});}
            var Q32;
            {var subQ0=sQuery(id+"F12.wireOp",EDGE,"E65");var subQ1=sQuery(id+"F50.wireOp",EDGE,"E158");var subQ2=sQuery(id+"F50.wireOp",EDGE,"E166");Q32=makeQuery(id+"F51.boolean.opBoolean","COPY",EDGE,{"disambiguationData":[topologyDisambiguationEdgeConnected([makeQuery(id+"F13.boolean.opBoolean","COPY",FACE,{"derivedFrom":makeQuery(id+"F13.opExtrude","SWEPT_FACE",FACE,{"disambiguationData":[OSD([subQ0])]})})])],"derivedFrom":makeQuery(id+"F51.opExtrude","SWEPT_EDGE",EDGE,{"disambiguationData":[OSD([subQ0,subQ1,subQ2])]})});}
            var Q33;
            Q33=makeQuery(id+"F3.boolean.opBoolean","INTERSECT",EDGE,{"derivedFrom":[makeQuery(id+"F1.opExtrude","SWEPT_FACE",FACE,{"disambiguationData":[OSD([sQuery(id+"F0.wireOp",EDGE,"E16"),sQuery(id+"F0.wireOp",EDGE,"E25.trimOffspring"),sQuery(id+"F0.wireOp",EDGE,"E28")])]}),makeQuery(id+"F3.opExtrude","SWEPT_FACE",FACE,{"disambiguationData":[OSD([sQuery(id+"F2.wireOp",EDGE,"E40")])]})]});
            var Q34;
            {var subQ5=sQuery(id+"F0.wireOp",EDGE,"E29");var subQ8=sQuery(id+"F0.wireOp",EDGE,"E23.trimOffspring");var subQ12=sQuery(id+"F0.wireOp",EDGE,"E15");var subQ20=sQuery(id+"F2.wireOp",EDGE,"E41");Q34=makeQuery(id+"F46.boolean.opBoolean","INTERSECT",EDGE,{"derivedFrom":[makeQuery(id+"F3.boolean.opBoolean","SPLIT",FACE,{"disambiguationData":[TD([makeQuery(id+"F3.opExtrude","SWEPT_FACE",FACE,{"disambiguationData":[OSD([subQ20])]})])],"derivedFrom":makeQuery(id+"F1.opExtrude","SWEPT_FACE",FACE,{"disambiguationData":[OSD([subQ12,subQ8,subQ5])]})}),makeQuery(id+"F46.opExtrude","SWEPT_FACE",FACE,{"disambiguationData":[OSD([sQuery(id+"F45.wireOp",EDGE,"E125")])]})]});}
            var Q35;
            {var subQ5=sQuery(id+"F0.wireOp",EDGE,"E28");var subQ7=sQuery(id+"F0.wireOp",EDGE,"E25.trimOffspring");var subQ12=sQuery(id+"F0.wireOp",EDGE,"E16");var subQ20=sQuery(id+"F2.wireOp",EDGE,"E40");Q35=makeQuery(id+"F46.boolean.opBoolean","INTERSECT",EDGE,{"derivedFrom":[makeQuery(id+"F3.boolean.opBoolean","SPLIT",FACE,{"disambiguationData":[TD([makeQuery(id+"F3.opExtrude","SWEPT_FACE",FACE,{"disambiguationData":[OSD([subQ20])]})])],"derivedFrom":makeQuery(id+"F1.opExtrude","SWEPT_FACE",FACE,{"disambiguationData":[OSD([subQ12,subQ7,subQ5])]})}),makeQuery(id+"F46.opExtrude","SWEPT_FACE",FACE,{"disambiguationData":[OSD([sQuery(id+"F45.wireOp",EDGE,"E125")])]})]});}
            var Q36;
            Q36=makeQuery(id+"F51.boolean.opBoolean","COPY",EDGE,{"derivedFrom":makeQuery(id+"F51.opExtrude","SWEPT_EDGE",EDGE,{"disambiguationData":[OSD([sQuery(id+"F50.wireOp",EDGE,"E154"),sQuery(id+"F50.wireOp",EDGE,"E156")])]})});
            var Q37;
            Q37=makeQuery(id+"F51.boolean.opBoolean","COPY",EDGE,{"derivedFrom":makeQuery(id+"F51.opExtrude","SWEPT_EDGE",EDGE,{"disambiguationData":[OSD([sQuery(id+"F50.wireOp",EDGE,"E155"),sQuery(id+"F50.wireOp",EDGE,"E161")])]})});
            var Q38;
            Q38=makeQuery(id+"F51.boolean.opBoolean","COPY",EDGE,{"derivedFrom":makeQuery(id+"F51.opExtrude","SWEPT_EDGE",EDGE,{"disambiguationData":[OSD([sQuery(id+"F50.wireOp",EDGE,"E157"),sQuery(id+"F50.wireOp",EDGE,"E158")])]})});
            var Q39;
            Q39=makeQuery(id+"F51.boolean.opBoolean","COPY",EDGE,{"derivedFrom":makeQuery(id+"F51.opExtrude","SWEPT_EDGE",EDGE,{"disambiguationData":[OSD([sQuery(id+"F50.wireOp",EDGE,"E159"),sQuery(id+"F50.wireOp",EDGE,"E160")])]})});
            fillet(context, id + "F52", {"entities" : qUnion([Q0, Q1, Q2, Q3, Q4, Q5, Q6, Q7, Q8, Q9, Q10, Q11, Q12, Q13, Q14, Q15, Q16, Q17, Q18, Q19, Q20, Q21, Q22, Q23, Q24, Q25, Q26, Q27, Q28, Q29, Q30, Q31, Q32, Q33, Q34, Q35, Q36, Q37, Q38, Q39]), "radius" : 1 * mm, "tangentPropagation" : true, "allowEdgeOverflow" : false});
        }
        {
            var Q0;
            {var subQ0=sQuery(id+"F2.wireOp",EDGE,"E41");var subQ1=sQuery(id+"F2.wireOp",EDGE,"E35");var subQ2=sQuery(id+"F2.wireOp",EDGE,"E42");Q0=makeQuery(id+"F17.boolean.opBoolean","SPLIT",FACE,{"disambiguationData":[TD([makeQuery(id+"F17.opExtrude","SWEPT_FACE",FACE,{"disambiguationData":[OSD([sQuery(id+"F16.wireOp",EDGE,"E79")])]})])],"derivedFrom":makeQuery(id+"F13.boolean.opBoolean","SPLIT",FACE,{"disambiguationData":[TD([makeQuery(id+"F1.opExtrude","SWEPT_FACE",FACE,{"disambiguationData":[OSD([sQuery(id+"F0.wireOp",EDGE,"E0.left")])]})])],"derivedFrom":makeQuery(id+"F3.opExtrude","CAP_FACE",FACE,{"disambiguationData":[OSD([sQuery(id+"F2.wireOp",EDGE,"E34"),subQ1,sQuery(id+"F2.wireOp",EDGE,"E36"),sQuery(id+"F2.wireOp",EDGE,"E37"),sQuery(id+"F2.wireOp",EDGE,"E38"),sQuery(id+"F2.wireOp",EDGE,"E39"),sQuery(id+"F2.wireOp",EDGE,"E40"),subQ0,subQ2,sQuery(id+"F2.wireOp",EDGE,"E43"),sQuery(id+"F2.wireOp",EDGE,"E44"),sQuery(id+"F2.wireOp",EDGE,"E45")])],"isStart":false})})});}
            var Q1;
            {var subQ0=sQuery(id+"F2.wireOp",EDGE,"E40");var subQ1=sQuery(id+"F2.wireOp",EDGE,"E39");var subQ2=sQuery(id+"F2.wireOp",EDGE,"E36");Q1=makeQuery(id+"F23.boolean.opBoolean","SPLIT",FACE,{"disambiguationData":[TD([makeQuery(id+"F23.opExtrude","SWEPT_FACE",FACE,{"disambiguationData":[OSD([sQuery(id+"F22.wireOp",EDGE,"E88")])]})])],"derivedFrom":makeQuery(id+"F13.boolean.opBoolean","SPLIT",FACE,{"disambiguationData":[TD([makeQuery(id+"F1.opExtrude","SWEPT_FACE",FACE,{"disambiguationData":[OSD([sQuery(id+"F0.wireOp",EDGE,"E27")])]})])],"derivedFrom":makeQuery(id+"F3.opExtrude","CAP_FACE",FACE,{"disambiguationData":[OSD([sQuery(id+"F2.wireOp",EDGE,"E34"),sQuery(id+"F2.wireOp",EDGE,"E35"),subQ2,sQuery(id+"F2.wireOp",EDGE,"E37"),sQuery(id+"F2.wireOp",EDGE,"E38"),subQ1,subQ0,sQuery(id+"F2.wireOp",EDGE,"E41"),sQuery(id+"F2.wireOp",EDGE,"E42"),sQuery(id+"F2.wireOp",EDGE,"E43"),sQuery(id+"F2.wireOp",EDGE,"E44"),sQuery(id+"F2.wireOp",EDGE,"E45")])],"isStart":false})})});}
            var Q2;
            {var subQ0=sQuery(id+"F2.wireOp",EDGE,"E45");var subQ1=sQuery(id+"F2.wireOp",EDGE,"E37");var subQ2=sQuery(id+"F2.wireOp",EDGE,"E38");Q2=makeQuery(id+"F21.boolean.opBoolean","SPLIT",FACE,{"disambiguationData":[TD([makeQuery(id+"F21.opExtrude","SWEPT_FACE",FACE,{"disambiguationData":[OSD([sQuery(id+"F20.wireOp",EDGE,"E85")])]})])],"derivedFrom":makeQuery(id+"F13.boolean.opBoolean","SPLIT",FACE,{"disambiguationData":[TD([makeQuery(id+"F1.opExtrude","SWEPT_FACE",FACE,{"disambiguationData":[OSD([sQuery(id+"F0.wireOp",EDGE,"E0.right")])]})])],"derivedFrom":makeQuery(id+"F3.opExtrude","CAP_FACE",FACE,{"disambiguationData":[OSD([sQuery(id+"F2.wireOp",EDGE,"E34"),sQuery(id+"F2.wireOp",EDGE,"E35"),sQuery(id+"F2.wireOp",EDGE,"E36"),subQ1,subQ2,sQuery(id+"F2.wireOp",EDGE,"E39"),sQuery(id+"F2.wireOp",EDGE,"E40"),sQuery(id+"F2.wireOp",EDGE,"E41"),sQuery(id+"F2.wireOp",EDGE,"E42"),sQuery(id+"F2.wireOp",EDGE,"E43"),sQuery(id+"F2.wireOp",EDGE,"E44"),subQ0])],"isStart":false})})});}
            var Q3;
            {var subQ0=sQuery(id+"F2.wireOp",EDGE,"E43");var subQ1=sQuery(id+"F2.wireOp",EDGE,"E34");var subQ2=sQuery(id+"F2.wireOp",EDGE,"E44");Q3=makeQuery(id+"F19.boolean.opBoolean","SPLIT",FACE,{"disambiguationData":[TD([makeQuery(id+"F19.opExtrude","SWEPT_FACE",FACE,{"disambiguationData":[OSD([sQuery(id+"F18.wireOp",EDGE,"E82")])]})])],"derivedFrom":makeQuery(id+"F13.boolean.opBoolean","SPLIT",FACE,{"disambiguationData":[TD([makeQuery(id+"F1.opExtrude","SWEPT_FACE",FACE,{"disambiguationData":[OSD([sQuery(id+"F0.wireOp",EDGE,"E0.top")])]})])],"derivedFrom":makeQuery(id+"F3.opExtrude","CAP_FACE",FACE,{"disambiguationData":[OSD([subQ1,sQuery(id+"F2.wireOp",EDGE,"E35"),sQuery(id+"F2.wireOp",EDGE,"E36"),sQuery(id+"F2.wireOp",EDGE,"E37"),sQuery(id+"F2.wireOp",EDGE,"E38"),sQuery(id+"F2.wireOp",EDGE,"E39"),sQuery(id+"F2.wireOp",EDGE,"E40"),sQuery(id+"F2.wireOp",EDGE,"E41"),sQuery(id+"F2.wireOp",EDGE,"E42"),subQ0,subQ2,sQuery(id+"F2.wireOp",EDGE,"E45")])],"isStart":false})})});}
            extrude(context, id + "F53", {"entities" : qUnion([Q0, Q1, Q2, Q3]), "operationType" : NewBodyOperationType.REMOVE, "endBound" : BoundingType.UP_TO_NEXT, "oppositeDirection" : true, "depth" : 25 * mm});
        }
        {
            var Q0;
            Q0=makeQuery(id+"F3.boolean.opBoolean","INTERSECT",EDGE,{"derivedFrom":[makeQuery(id+"F1.opExtrude","CAP_FACE",FACE,{"disambiguationData":[OSD([sQuery(id+"F0.wireOp",EDGE,"E0.top"),sQuery(id+"F0.wireOp",EDGE,"E0.left"),sQuery(id+"F0.wireOp",EDGE,"E0.right"),sQuery(id+"F0.wireOp",EDGE,"E6"),sQuery(id+"F0.wireOp",EDGE,"E10"),sQuery(id+"F0.wireOp",EDGE,"E11"),sQuery(id+"F0.wireOp",EDGE,"E12"),sQuery(id+"F0.wireOp",EDGE,"E16"),sQuery(id+"F0.wireOp",EDGE,"E15"),sQuery(id+"F0.wireOp",EDGE,"E18"),sQuery(id+"F0.wireOp",EDGE,"E17"),sQuery(id+"F0.wireOp",EDGE,"E22.trimOffspring"),sQuery(id+"F0.wireOp",EDGE,"E23.trimOffspring"),sQuery(id+"F0.wireOp",EDGE,"E24.trimOffspring"),sQuery(id+"F0.wireOp",EDGE,"E25.trimOffspring"),sQuery(id+"F0.wireOp",EDGE,"E27"),sQuery(id+"F0.wireOp",EDGE,"E28"),sQuery(id+"F0.wireOp",EDGE,"E29"),sQuery(id+"F0.wireOp",EDGE,"E30"),sQuery(id+"F0.wireOp",EDGE,"E31")])],"isStart":true}),makeQuery(id+"F3.opExtrude","SWEPT_FACE",FACE,{"disambiguationData":[OSD([sQuery(id+"F2.wireOp",EDGE,"E41")])]})]});
            var Q1;
            Q1=makeQuery(id+"F3.boolean.opBoolean","INTERSECT",EDGE,{"derivedFrom":[makeQuery(id+"F1.opExtrude","CAP_FACE",FACE,{"disambiguationData":[OSD([sQuery(id+"F0.wireOp",EDGE,"E0.top"),sQuery(id+"F0.wireOp",EDGE,"E0.left"),sQuery(id+"F0.wireOp",EDGE,"E0.right"),sQuery(id+"F0.wireOp",EDGE,"E6"),sQuery(id+"F0.wireOp",EDGE,"E10"),sQuery(id+"F0.wireOp",EDGE,"E11"),sQuery(id+"F0.wireOp",EDGE,"E12"),sQuery(id+"F0.wireOp",EDGE,"E16"),sQuery(id+"F0.wireOp",EDGE,"E15"),sQuery(id+"F0.wireOp",EDGE,"E18"),sQuery(id+"F0.wireOp",EDGE,"E17"),sQuery(id+"F0.wireOp",EDGE,"E22.trimOffspring"),sQuery(id+"F0.wireOp",EDGE,"E23.trimOffspring"),sQuery(id+"F0.wireOp",EDGE,"E24.trimOffspring"),sQuery(id+"F0.wireOp",EDGE,"E25.trimOffspring"),sQuery(id+"F0.wireOp",EDGE,"E27"),sQuery(id+"F0.wireOp",EDGE,"E28"),sQuery(id+"F0.wireOp",EDGE,"E29"),sQuery(id+"F0.wireOp",EDGE,"E30"),sQuery(id+"F0.wireOp",EDGE,"E31")])],"isStart":true}),makeQuery(id+"F3.opExtrude","SWEPT_FACE",FACE,{"disambiguationData":[OSD([sQuery(id+"F2.wireOp",EDGE,"E42")])]})]});
            var Q2;
            Q2=makeQuery(id+"F3.boolean.opBoolean","INTERSECT",EDGE,{"derivedFrom":[makeQuery(id+"F1.opExtrude","CAP_FACE",FACE,{"disambiguationData":[OSD([sQuery(id+"F0.wireOp",EDGE,"E0.top"),sQuery(id+"F0.wireOp",EDGE,"E0.left"),sQuery(id+"F0.wireOp",EDGE,"E0.right"),sQuery(id+"F0.wireOp",EDGE,"E6"),sQuery(id+"F0.wireOp",EDGE,"E10"),sQuery(id+"F0.wireOp",EDGE,"E11"),sQuery(id+"F0.wireOp",EDGE,"E12"),sQuery(id+"F0.wireOp",EDGE,"E16"),sQuery(id+"F0.wireOp",EDGE,"E15"),sQuery(id+"F0.wireOp",EDGE,"E18"),sQuery(id+"F0.wireOp",EDGE,"E17"),sQuery(id+"F0.wireOp",EDGE,"E22.trimOffspring"),sQuery(id+"F0.wireOp",EDGE,"E23.trimOffspring"),sQuery(id+"F0.wireOp",EDGE,"E24.trimOffspring"),sQuery(id+"F0.wireOp",EDGE,"E25.trimOffspring"),sQuery(id+"F0.wireOp",EDGE,"E27"),sQuery(id+"F0.wireOp",EDGE,"E28"),sQuery(id+"F0.wireOp",EDGE,"E29"),sQuery(id+"F0.wireOp",EDGE,"E30"),sQuery(id+"F0.wireOp",EDGE,"E31")])],"isStart":true}),makeQuery(id+"F3.opExtrude","SWEPT_FACE",FACE,{"disambiguationData":[OSD([sQuery(id+"F2.wireOp",EDGE,"E43")])]})]});
            var Q3;
            Q3=makeQuery(id+"F3.boolean.opBoolean","INTERSECT",EDGE,{"derivedFrom":[makeQuery(id+"F1.opExtrude","CAP_FACE",FACE,{"disambiguationData":[OSD([sQuery(id+"F0.wireOp",EDGE,"E0.top"),sQuery(id+"F0.wireOp",EDGE,"E0.left"),sQuery(id+"F0.wireOp",EDGE,"E0.right"),sQuery(id+"F0.wireOp",EDGE,"E6"),sQuery(id+"F0.wireOp",EDGE,"E10"),sQuery(id+"F0.wireOp",EDGE,"E11"),sQuery(id+"F0.wireOp",EDGE,"E12"),sQuery(id+"F0.wireOp",EDGE,"E16"),sQuery(id+"F0.wireOp",EDGE,"E15"),sQuery(id+"F0.wireOp",EDGE,"E18"),sQuery(id+"F0.wireOp",EDGE,"E17"),sQuery(id+"F0.wireOp",EDGE,"E22.trimOffspring"),sQuery(id+"F0.wireOp",EDGE,"E23.trimOffspring"),sQuery(id+"F0.wireOp",EDGE,"E24.trimOffspring"),sQuery(id+"F0.wireOp",EDGE,"E25.trimOffspring"),sQuery(id+"F0.wireOp",EDGE,"E27"),sQuery(id+"F0.wireOp",EDGE,"E28"),sQuery(id+"F0.wireOp",EDGE,"E29"),sQuery(id+"F0.wireOp",EDGE,"E30"),sQuery(id+"F0.wireOp",EDGE,"E31")])],"isStart":true}),makeQuery(id+"F3.opExtrude","SWEPT_FACE",FACE,{"disambiguationData":[OSD([sQuery(id+"F2.wireOp",EDGE,"E44")])]})]});
            var Q4;
            Q4=makeQuery(id+"F3.boolean.opBoolean","INTERSECT",EDGE,{"derivedFrom":[makeQuery(id+"F1.opExtrude","CAP_FACE",FACE,{"disambiguationData":[OSD([sQuery(id+"F0.wireOp",EDGE,"E0.top"),sQuery(id+"F0.wireOp",EDGE,"E0.left"),sQuery(id+"F0.wireOp",EDGE,"E0.right"),sQuery(id+"F0.wireOp",EDGE,"E6"),sQuery(id+"F0.wireOp",EDGE,"E10"),sQuery(id+"F0.wireOp",EDGE,"E11"),sQuery(id+"F0.wireOp",EDGE,"E12"),sQuery(id+"F0.wireOp",EDGE,"E16"),sQuery(id+"F0.wireOp",EDGE,"E15"),sQuery(id+"F0.wireOp",EDGE,"E18"),sQuery(id+"F0.wireOp",EDGE,"E17"),sQuery(id+"F0.wireOp",EDGE,"E22.trimOffspring"),sQuery(id+"F0.wireOp",EDGE,"E23.trimOffspring"),sQuery(id+"F0.wireOp",EDGE,"E24.trimOffspring"),sQuery(id+"F0.wireOp",EDGE,"E25.trimOffspring"),sQuery(id+"F0.wireOp",EDGE,"E27"),sQuery(id+"F0.wireOp",EDGE,"E28"),sQuery(id+"F0.wireOp",EDGE,"E29"),sQuery(id+"F0.wireOp",EDGE,"E30"),sQuery(id+"F0.wireOp",EDGE,"E31")])],"isStart":true}),makeQuery(id+"F3.opExtrude","SWEPT_FACE",FACE,{"disambiguationData":[OSD([sQuery(id+"F2.wireOp",EDGE,"E45")])]})]});
            var Q5;
            Q5=makeQuery(id+"F3.boolean.opBoolean","INTERSECT",EDGE,{"derivedFrom":[makeQuery(id+"F1.opExtrude","CAP_FACE",FACE,{"disambiguationData":[OSD([sQuery(id+"F0.wireOp",EDGE,"E0.top"),sQuery(id+"F0.wireOp",EDGE,"E0.left"),sQuery(id+"F0.wireOp",EDGE,"E0.right"),sQuery(id+"F0.wireOp",EDGE,"E6"),sQuery(id+"F0.wireOp",EDGE,"E10"),sQuery(id+"F0.wireOp",EDGE,"E11"),sQuery(id+"F0.wireOp",EDGE,"E12"),sQuery(id+"F0.wireOp",EDGE,"E16"),sQuery(id+"F0.wireOp",EDGE,"E15"),sQuery(id+"F0.wireOp",EDGE,"E18"),sQuery(id+"F0.wireOp",EDGE,"E17"),sQuery(id+"F0.wireOp",EDGE,"E22.trimOffspring"),sQuery(id+"F0.wireOp",EDGE,"E23.trimOffspring"),sQuery(id+"F0.wireOp",EDGE,"E24.trimOffspring"),sQuery(id+"F0.wireOp",EDGE,"E25.trimOffspring"),sQuery(id+"F0.wireOp",EDGE,"E27"),sQuery(id+"F0.wireOp",EDGE,"E28"),sQuery(id+"F0.wireOp",EDGE,"E29"),sQuery(id+"F0.wireOp",EDGE,"E30"),sQuery(id+"F0.wireOp",EDGE,"E31")])],"isStart":true}),makeQuery(id+"F3.opExtrude","SWEPT_FACE",FACE,{"disambiguationData":[OSD([sQuery(id+"F2.wireOp",EDGE,"E38")])]})]});
            var Q6;
            Q6=makeQuery(id+"F3.boolean.opBoolean","INTERSECT",EDGE,{"derivedFrom":[makeQuery(id+"F1.opExtrude","CAP_FACE",FACE,{"disambiguationData":[OSD([sQuery(id+"F0.wireOp",EDGE,"E0.top"),sQuery(id+"F0.wireOp",EDGE,"E0.left"),sQuery(id+"F0.wireOp",EDGE,"E0.right"),sQuery(id+"F0.wireOp",EDGE,"E6"),sQuery(id+"F0.wireOp",EDGE,"E10"),sQuery(id+"F0.wireOp",EDGE,"E11"),sQuery(id+"F0.wireOp",EDGE,"E12"),sQuery(id+"F0.wireOp",EDGE,"E16"),sQuery(id+"F0.wireOp",EDGE,"E15"),sQuery(id+"F0.wireOp",EDGE,"E18"),sQuery(id+"F0.wireOp",EDGE,"E17"),sQuery(id+"F0.wireOp",EDGE,"E22.trimOffspring"),sQuery(id+"F0.wireOp",EDGE,"E23.trimOffspring"),sQuery(id+"F0.wireOp",EDGE,"E24.trimOffspring"),sQuery(id+"F0.wireOp",EDGE,"E25.trimOffspring"),sQuery(id+"F0.wireOp",EDGE,"E27"),sQuery(id+"F0.wireOp",EDGE,"E28"),sQuery(id+"F0.wireOp",EDGE,"E29"),sQuery(id+"F0.wireOp",EDGE,"E30"),sQuery(id+"F0.wireOp",EDGE,"E31")])],"isStart":true}),makeQuery(id+"F3.opExtrude","SWEPT_FACE",FACE,{"disambiguationData":[OSD([sQuery(id+"F2.wireOp",EDGE,"E39")])]})]});
            var Q7;
            Q7=makeQuery(id+"F3.boolean.opBoolean","INTERSECT",EDGE,{"derivedFrom":[makeQuery(id+"F1.opExtrude","CAP_FACE",FACE,{"disambiguationData":[OSD([sQuery(id+"F0.wireOp",EDGE,"E0.top"),sQuery(id+"F0.wireOp",EDGE,"E0.left"),sQuery(id+"F0.wireOp",EDGE,"E0.right"),sQuery(id+"F0.wireOp",EDGE,"E6"),sQuery(id+"F0.wireOp",EDGE,"E10"),sQuery(id+"F0.wireOp",EDGE,"E11"),sQuery(id+"F0.wireOp",EDGE,"E12"),sQuery(id+"F0.wireOp",EDGE,"E16"),sQuery(id+"F0.wireOp",EDGE,"E15"),sQuery(id+"F0.wireOp",EDGE,"E18"),sQuery(id+"F0.wireOp",EDGE,"E17"),sQuery(id+"F0.wireOp",EDGE,"E22.trimOffspring"),sQuery(id+"F0.wireOp",EDGE,"E23.trimOffspring"),sQuery(id+"F0.wireOp",EDGE,"E24.trimOffspring"),sQuery(id+"F0.wireOp",EDGE,"E25.trimOffspring"),sQuery(id+"F0.wireOp",EDGE,"E27"),sQuery(id+"F0.wireOp",EDGE,"E28"),sQuery(id+"F0.wireOp",EDGE,"E29"),sQuery(id+"F0.wireOp",EDGE,"E30"),sQuery(id+"F0.wireOp",EDGE,"E31")])],"isStart":true}),makeQuery(id+"F3.opExtrude","SWEPT_FACE",FACE,{"disambiguationData":[OSD([sQuery(id+"F2.wireOp",EDGE,"E40")])]})]});
            chamfer(context, id + "F54", {"entities" : qUnion([Q0, Q1, Q2, Q3, Q4, Q5, Q6, Q7]), "chamferType" : ChamferType.TWO_OFFSETS, "width1" : 5 * mm, "oppositeDirection" : false, "width2" : 3 * mm, "tangentPropagation" : true});
        }
    });
